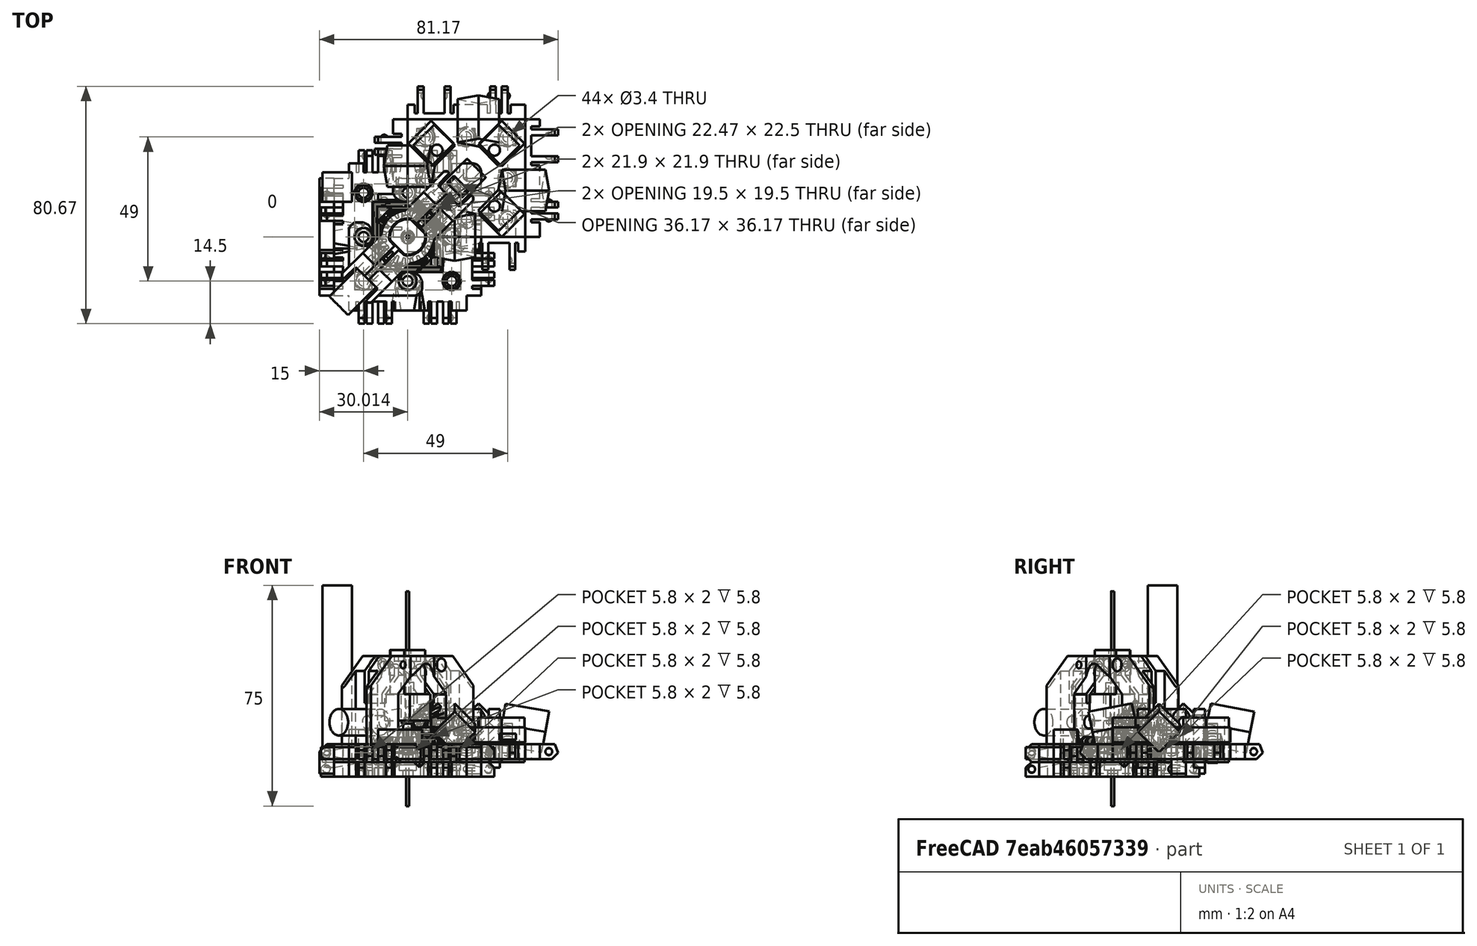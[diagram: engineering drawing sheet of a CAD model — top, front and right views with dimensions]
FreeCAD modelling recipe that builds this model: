
FCSTD DOCUMENT  (FreeCAD 0.18.4R)
Label: Robot-0.1
License: All rights reserved
LicenseURL: http://en.wikipedia.org/wiki/All_rights_reserved
objects: Part::Box×350, Part::Cut×132, Part::Sphere×107, Part::MultiFuse×98, Part::Cylinder×68, Part::Fuse×44, Part::Chamfer×23, Part::Feature×12, Drawing::FeatureViewAnnotation×10, Part::Fillet×7, App::DocumentObjectGroup×4, Part::MultiCommon×4, Drawing::FeaturePage×2, Part::FeaturePython×2, Part::Cone×2, Part::Mirroring×1
note: 850 computed .brp shape members not serialized (recipe doc carries the construction recipe); baked Part::Feature solids carry a one-line shape summary decoded from their .brp

FEATURE [Part::Box] Box  label="Cube"
  AttacherType = Attacher::AttachEngine3D
  Height = 5
  Length = 40
  Placement = pos=(-20,-20,-2) rot=(0,0,1;0rad)
  Width = 40
FEATURE [Part::Sphere] Sphere003  label="Mag Hole 3"
  Angle1 = -90
  Angle2 = 90
  Angle3 = 360
  AttacherType = Attacher::AttachEngine3D
  Placement = pos=(-15,15,1.7) rot=(0,0,1;0rad)
  Radius = 2.83
FEATURE [Part::Sphere] Sphere005  label="Mag Hole 2"
  Angle1 = -90
  Angle2 = 90
  Angle3 = 360
  AttacherType = Attacher::AttachEngine3D
  Placement = pos=(15,0,1.7) rot=(0,0,1;0rad)
  Radius = 2.825
FEATURE [Part::Sphere] Sphere  label="Mag Hole"
  Angle1 = -90
  Angle2 = 90
  Angle3 = 360
  AttacherType = Attacher::AttachEngine3D
  Placement = pos=(-15,-15,1.7) rot=(0,0,1;0rad)
  Radius = 2.83
FEATURE [Part::MultiFuse] Fusion004  label="Ball Holes"
  Shapes = -> [Sphere,Sphere005,Sphere003]
FEATURE [Part::Cut] Cut003
  Base = -> Box
  Tool = -> Fusion004
FEATURE [Part::Box] Box001  label="Cube001"
  AttacherType = Attacher::AttachEngine3D
  Height = 7
  Length = 5
  Placement = pos=(-5,0,-2) rot=(0,0,1;0rad)
  Width = 40
FEATURE [Part::Box] Box002  label="Cube002"
  AttacherType = Attacher::AttachEngine3D
  Height = 7
  Length = 10
  Placement = pos=(-15,6,-2) rot=(0,0,1;0rad)
  Width = 2
FEATURE [Part::Box] Box003  label="Cube003"
  AttacherType = Attacher::AttachEngine3D
  Height = 7
  Length = 10
  Placement = pos=(-15,10,-2) rot=(0,0,1;0rad)
  Width = 2
FEATURE [Part::Box] Box004  label="Cube004"
  AttacherType = Attacher::AttachEngine3D
  Height = 7
  Length = 10
  Placement = pos=(-15,25.4,-2) rot=(0,0,1;0rad)
  Width = 2
FEATURE [Part::Box] Box005  label="Cube005"
  AttacherType = Attacher::AttachEngine3D
  Height = 7
  Length = 10
  Placement = pos=(-15,34.6,-2) rot=(0,0,1;0rad)
  Width = 2
FEATURE [Part::Sphere] Sphere008
  Angle1 = -90
  Angle2 = 90
  Angle3 = 360
  AttacherType = Attacher::AttachEngine3D
  Placement = pos=(-7.5,6.5,0.5) rot=(0,0,1;0rad)
  Radius = 1.25
FEATURE [Part::Box] Box006  label="Chamfer Cube"
  AttacherType = Attacher::AttachEngine3D
  Height = 10
  Length = 13
  Placement = pos=(-11.69,0,-1.19) rot=(0,-1,0;0.785398rad)
  Width = 40
FEATURE [Part::Sphere] Sphere009
  Angle1 = -90
  Angle2 = 90
  Angle3 = 360
  AttacherType = Attacher::AttachEngine3D
  Placement = pos=(-7.5,11.5,0.5) rot=(0,0,1;0rad)
  Radius = 1.25
FEATURE [Part::Sphere] Sphere010
  Angle1 = -90
  Angle2 = 90
  Angle3 = 360
  AttacherType = Attacher::AttachEngine3D
  Placement = pos=(-7.5,28,0.5) rot=(0,0,1;0rad)
  Radius = 1.5
FEATURE [Part::Sphere] Sphere011
  Angle1 = -90
  Angle2 = 90
  Angle3 = 360
  AttacherType = Attacher::AttachEngine3D
  Placement = pos=(-7.5,34,0.5) rot=(0,0,1;0rad)
  Radius = 1.5
FEATURE [Part::Box] Box007  label="Cube007"
  AttacherType = Attacher::AttachEngine3D
  Height = 7
  Length = 4
  Placement = pos=(-6,5,-2) rot=(0,0,1;0rad)
  Width = 1
FEATURE [Part::Box] Box008  label="Cube008"
  AttacherType = Attacher::AttachEngine3D
  Height = 7
  Length = 4
  Placement = pos=(-6,8,-2) rot=(0,0,1;0rad)
  Width = 2
FEATURE [Part::Box] Box009  label="Cube009"
  AttacherType = Attacher::AttachEngine3D
  Height = 7
  Length = 4
  Placement = pos=(-6,12,-2) rot=(0,0,1;0rad)
  Width = 1
FEATURE [Part::Box] Box010  label="Cube010"
  AttacherType = Attacher::AttachEngine3D
  Height = 7
  Length = 4
  Placement = pos=(-6,24.4,-2) rot=(0,0,1;0rad)
  Width = 1
FEATURE [Part::Box] Box011  label="Cube011"
  AttacherType = Attacher::AttachEngine3D
  Height = 7
  Length = 4
  Placement = pos=(-6,36.6,-2) rot=(0,0,1;0rad)
  Width = 1
FEATURE [Part::Box] Box012  label="Cube012"
  AttacherType = Attacher::AttachEngine3D
  Height = 7
  Length = 4
  Placement = pos=(-6,27.4,-2) rot=(0,0,1;0rad)
  Width = 7.2
FEATURE [Part::MultiFuse] Fusion003  label="Extra Holes for Clips"
  Shapes = -> [Box012,Box009,Box011,Box008,Box010,Box007]
FEATURE [Part::Box] Box013  label="Re-level Edge Clip Block"
  AttacherType = Attacher::AttachEngine3D
  Height = 10
  Length = 20
  Placement = pos=(-19,-2,3) rot=(0,0,1;0rad)
  Width = 44
FEATURE [Part::Box] Box014  label="Cube014"
  AttacherType = Attacher::AttachEngine3D
  Height = 7
  Length = 10
  Placement = pos=(-10,34.6,0) rot=(0,0,1;0rad)
  Width = 2
FEATURE [Part::Box] Box015  label="Cube015"
  AttacherType = Attacher::AttachEngine3D
  Height = 7
  Length = 5
  Width = 40
FEATURE [Part::Box] Box016  label="Cube016"
  AttacherType = Attacher::AttachEngine3D
  Height = 7
  Length = 10
  Placement = pos=(-10,25.4,0) rot=(0,0,1;0rad)
  Width = 2
FEATURE [Part::Box] Box017  label="Cube017"
  AttacherType = Attacher::AttachEngine3D
  Height = 7
  Length = 10
  Placement = pos=(-10,10,0) rot=(0,0,1;0rad)
  Width = 2
FEATURE [Part::Box] Box018  label="Cube018"
  AttacherType = Attacher::AttachEngine3D
  Height = 7
  Length = 10
  Placement = pos=(-10,6,0) rot=(0,0,1;0rad)
  Width = 2
FEATURE [Part::Sphere] Sphere012
  Angle1 = -90
  Angle2 = 90
  Angle3 = 360
  AttacherType = Attacher::AttachEngine3D
  Placement = pos=(-3,6.5,2.5) rot=(0,0,1;0rad)
  Radius = 1.25
FEATURE [Part::Box] Box019  label="Cube019"
  AttacherType = Attacher::AttachEngine3D
  Height = 10
  Length = 13
  Placement = pos=(-10.19,0,-1.19) rot=(0,-1,0;0.785398rad)
  Width = 40
FEATURE [Part::Sphere] Sphere013
  Angle1 = -90
  Angle2 = 90
  Angle3 = 360
  AttacherType = Attacher::AttachEngine3D
  Placement = pos=(-3,11.5,2.5) rot=(0,0,1;0rad)
  Radius = 1.25
FEATURE [Part::Sphere] Sphere014
  Angle1 = -90
  Angle2 = 90
  Angle3 = 360
  AttacherType = Attacher::AttachEngine3D
  Placement = pos=(-3,28,2.5) rot=(0,0,1;0rad)
  Radius = 1.5
FEATURE [Part::Sphere] Sphere015
  Angle1 = -90
  Angle2 = 90
  Angle3 = 360
  AttacherType = Attacher::AttachEngine3D
  Placement = pos=(-3,34,2.5) rot=(0,0,1;0rad)
  Radius = 1.5
FEATURE [Part::MultiFuse] Fusion005
  Shapes = -> [Box015,Box018,Box017,Box016,Box014]
FEATURE [Part::Cut] Cut005
  Base = -> Fusion005
  Tool = -> Box019
FEATURE [Part::MultiFuse] Fusion006
  Shapes = -> [Sphere012,Sphere013,Cut005]
FEATURE [Part::MultiFuse] Fusion007
  Shapes = -> [Sphere015,Sphere014]
FEATURE [Part::Cut] Cut006
  Base = -> Fusion006
  Tool = -> Fusion007
FEATURE [Part::Chamfer] Chamfer002
  Base = -> Cut006
  Edges = 4 edges r=4: [Edge31,Edge37,Edge43,Edge46]
FEATURE [Part::Box] Box020  label="Cube020"
  AttacherType = Attacher::AttachEngine3D
  Height = 7
  Length = 4
  Placement = pos=(-1,5,0) rot=(0,0,1;0rad)
  Width = 1
FEATURE [Part::Box] Box021  label="Cube021"
  AttacherType = Attacher::AttachEngine3D
  Height = 7
  Length = 4
  Placement = pos=(-1,8,0) rot=(0,0,1;0rad)
  Width = 2
FEATURE [Part::Box] Box022  label="Cube022"
  AttacherType = Attacher::AttachEngine3D
  Height = 7
  Length = 4
  Placement = pos=(-1,12,0) rot=(0,0,1;0rad)
  Width = 1
FEATURE [Part::Box] Box023  label="Cube023"
  AttacherType = Attacher::AttachEngine3D
  Height = 7
  Length = 4
  Placement = pos=(-1,24.4,0) rot=(0,0,1;0rad)
  Width = 1
FEATURE [Part::Box] Box024  label="Cube024"
  AttacherType = Attacher::AttachEngine3D
  Height = 7
  Length = 4
  Placement = pos=(-1,36.6,0) rot=(0,0,1;0rad)
  Width = 1
FEATURE [Part::Box] Box025  label="Cube025"
  AttacherType = Attacher::AttachEngine3D
  Height = 7
  Length = 4
  Placement = pos=(-1,27.4,0) rot=(0,0,1;0rad)
  Width = 7.2
FEATURE [Part::MultiFuse] Fusion008
  Shapes = -> [Box025,Box022,Box024,Box021,Box023,Box020]
FEATURE [Part::Cut] Cut007
  Base = -> Chamfer002
  Placement = pos=(-5,40,3) rot=(1,0,0;3.14159rad)
  Tool = -> Fusion008
FEATURE [Part::Box] Box026  label="Cube026"
  AttacherType = Attacher::AttachEngine3D
  Height = 10
  Length = 12
  Placement = pos=(-11,-2,-12) rot=(0,0,1;0rad)
  Width = 44
FEATURE [Part::Cut] Cut008
  Base = -> Cut007
  Placement = pos=(40,0,0) rot=(0,0,1;1.5708rad)
  Tool = -> Box026
FEATURE [Part::Box] Box027  label="Cube027"
  AttacherType = Attacher::AttachEngine3D
  Height = 7
  Length = 4
  Placement = pos=(-1,12,0) rot=(0,0,1;0rad)
  Width = 1
FEATURE [Part::Box] Box028  label="Cube028"
  AttacherType = Attacher::AttachEngine3D
  Height = 10
  Length = 13
  Placement = pos=(-10.19,0,-1.19) rot=(0,-1,0;0.785398rad)
  Width = 40
FEATURE [Part::Box] Box029  label="Cube029"
  AttacherType = Attacher::AttachEngine3D
  Height = 7
  Length = 4
  Placement = pos=(-1,27.4,0) rot=(0,0,1;0rad)
  Width = 7.2
FEATURE [Part::Box] Box030  label="Cube030"
  AttacherType = Attacher::AttachEngine3D
  Height = 7
  Length = 4
  Placement = pos=(-1,5,0) rot=(0,0,1;0rad)
  Width = 1
FEATURE [Part::Box] Box031  label="Cube031"
  AttacherType = Attacher::AttachEngine3D
  Height = 7
  Length = 10
  Placement = pos=(-10,6,0) rot=(0,0,1;0rad)
  Width = 2
FEATURE [Part::Box] Box032  label="Cube032"
  AttacherType = Attacher::AttachEngine3D
  Height = 10
  Length = 12
  Placement = pos=(-11,-2,-12) rot=(0,0,1;0rad)
  Width = 44
FEATURE [Part::Sphere] Sphere016
  Angle1 = -90
  Angle2 = 90
  Angle3 = 360
  AttacherType = Attacher::AttachEngine3D
  Placement = pos=(-3,6.5,2.5) rot=(0,0,1;0rad)
  Radius = 1.25
FEATURE [Part::Box] Box033  label="Cube033"
  AttacherType = Attacher::AttachEngine3D
  Height = 7
  Length = 10
  Placement = pos=(-10,25.4,0) rot=(0,0,1;0rad)
  Width = 2
FEATURE [Part::Box] Box034  label="Cube034"
  AttacherType = Attacher::AttachEngine3D
  Height = 7
  Length = 10
  Placement = pos=(-10,10,0) rot=(0,0,1;0rad)
  Width = 2
FEATURE [Part::Sphere] Sphere017
  Angle1 = -90
  Angle2 = 90
  Angle3 = 360
  AttacherType = Attacher::AttachEngine3D
  Placement = pos=(-3,28,2.5) rot=(0,0,1;0rad)
  Radius = 1.5
FEATURE [Part::Sphere] Sphere018
  Angle1 = -90
  Angle2 = 90
  Angle3 = 360
  AttacherType = Attacher::AttachEngine3D
  Placement = pos=(-3,11.5,2.5) rot=(0,0,1;0rad)
  Radius = 1.25
FEATURE [Part::Box] Box035  label="Cube035"
  AttacherType = Attacher::AttachEngine3D
  Height = 7
  Length = 4
  Placement = pos=(-1,36.6,0) rot=(0,0,1;0rad)
  Width = 1
FEATURE [Part::Sphere] Sphere019
  Angle1 = -90
  Angle2 = 90
  Angle3 = 360
  AttacherType = Attacher::AttachEngine3D
  Placement = pos=(-3,34,2.5) rot=(0,0,1;0rad)
  Radius = 1.5
FEATURE [Part::MultiFuse] Fusion011
  Shapes = -> [Sphere019,Sphere017]
FEATURE [Part::Box] Box036  label="Cube036"
  AttacherType = Attacher::AttachEngine3D
  Height = 7
  Length = 4
  Placement = pos=(-1,8,0) rot=(0,0,1;0rad)
  Width = 2
FEATURE [Part::Box] Box037  label="Cube037"
  AttacherType = Attacher::AttachEngine3D
  Height = 7
  Length = 10
  Placement = pos=(-10,34.6,0) rot=(0,0,1;0rad)
  Width = 2
FEATURE [Part::Box] Box038  label="Cube038"
  AttacherType = Attacher::AttachEngine3D
  Height = 7
  Length = 4
  Placement = pos=(-1,24.4,0) rot=(0,0,1;0rad)
  Width = 1
FEATURE [Part::MultiFuse] Fusion009
  Shapes = -> [Box029,Box027,Box035,Box036,Box038,Box030]
FEATURE [Part::Box] Box039  label="Cube039"
  AttacherType = Attacher::AttachEngine3D
  Height = 7
  Length = 5
  Width = 40
FEATURE [Part::MultiFuse] Fusion012
  Shapes = -> [Box039,Box031,Box034,Box033,Box037]
FEATURE [Part::Cut] Cut011
  Base = -> Fusion012
  Tool = -> Box028
FEATURE [Part::MultiFuse] Fusion010
  Shapes = -> [Sphere016,Sphere018,Cut011]
FEATURE [Part::Cut] Cut012
  Base = -> Fusion010
  Tool = -> Fusion011
FEATURE [Part::Chamfer] Chamfer003
  Base = -> Cut012
  Edges = 4 edges r=4: [Edge31,Edge37,Edge43,Edge46]
FEATURE [Part::Cut] Cut010
  Base = -> Chamfer003
  Placement = pos=(-5,40,3) rot=(1,0,0;3.14159rad)
  Tool = -> Fusion009
FEATURE [Part::Cut] Cut009
  Base = -> Cut010
  Placement = pos=(40,40,0) rot=(0,0,1;3.14159rad)
  Tool = -> Box032
FEATURE [Part::Sphere] Sphere020
  Angle1 = -90
  Angle2 = 90
  Angle3 = 360
  AttacherType = Attacher::AttachEngine3D
  Placement = pos=(-3,11.5,2.5) rot=(0,0,1;0rad)
  Radius = 1.25
FEATURE [Part::Box] Box040  label="Cube040"
  AttacherType = Attacher::AttachEngine3D
  Height = 7
  Length = 10
  Placement = pos=(-10,6,0) rot=(0,0,1;0rad)
  Width = 2
FEATURE [Part::Box] Box041  label="Cube041"
  AttacherType = Attacher::AttachEngine3D
  Height = 7
  Length = 4
  Placement = pos=(-1,8,0) rot=(0,0,1;0rad)
  Width = 2
FEATURE [Part::Box] Box042  label="Cube042"
  AttacherType = Attacher::AttachEngine3D
  Height = 7
  Length = 10
  Placement = pos=(-10,10,0) rot=(0,0,1;0rad)
  Width = 2
FEATURE [Part::Box] Box043  label="Cube043"
  AttacherType = Attacher::AttachEngine3D
  Height = 10
  Length = 12
  Placement = pos=(-11,-2,-12) rot=(0,0,1;0rad)
  Width = 44
FEATURE [Part::Box] Box044  label="Cube044"
  AttacherType = Attacher::AttachEngine3D
  Height = 7
  Length = 4
  Placement = pos=(-1,5,0) rot=(0,0,1;0rad)
  Width = 1
FEATURE [Part::Sphere] Sphere021
  Angle1 = -90
  Angle2 = 90
  Angle3 = 360
  AttacherType = Attacher::AttachEngine3D
  Placement = pos=(-3,28,2.5) rot=(0,0,1;0rad)
  Radius = 1.5
FEATURE [Part::Sphere] Sphere022
  Angle1 = -90
  Angle2 = 90
  Angle3 = 360
  AttacherType = Attacher::AttachEngine3D
  Placement = pos=(-3,6.5,2.5) rot=(0,0,1;0rad)
  Radius = 1.25
FEATURE [Part::Sphere] Sphere023
  Angle1 = -90
  Angle2 = 90
  Angle3 = 360
  AttacherType = Attacher::AttachEngine3D
  Placement = pos=(-3,34,2.5) rot=(0,0,1;0rad)
  Radius = 1.5
FEATURE [Part::Box] Box045  label="Cube045"
  AttacherType = Attacher::AttachEngine3D
  Height = 7
  Length = 4
  Placement = pos=(-1,12,0) rot=(0,0,1;0rad)
  Width = 1
FEATURE [Part::Box] Box046  label="Cube046"
  AttacherType = Attacher::AttachEngine3D
  Height = 7
  Length = 5
  Width = 40
FEATURE [Part::Box] Box047  label="Cube047"
  AttacherType = Attacher::AttachEngine3D
  Height = 7
  Length = 4
  Placement = pos=(-1,36.6,0) rot=(0,0,1;0rad)
  Width = 1
FEATURE [Part::Box] Box048  label="Cube048"
  AttacherType = Attacher::AttachEngine3D
  Height = 7
  Length = 4
  Placement = pos=(-1,24.4,0) rot=(0,0,1;0rad)
  Width = 1
FEATURE [Part::Box] Box049  label="Cube049"
  AttacherType = Attacher::AttachEngine3D
  Height = 7
  Length = 10
  Placement = pos=(-10,25.4,0) rot=(0,0,1;0rad)
  Width = 2
FEATURE [Part::Box] Box050  label="Cube050"
  AttacherType = Attacher::AttachEngine3D
  Height = 10
  Length = 13
  Placement = pos=(-10.19,0,-1.19) rot=(0,-1,0;0.785398rad)
  Width = 40
FEATURE [Part::Box] Box051  label="Cube051"
  AttacherType = Attacher::AttachEngine3D
  Height = 7
  Length = 10
  Placement = pos=(-10,34.6,0) rot=(0,0,1;0rad)
  Width = 2
FEATURE [Part::MultiFuse] Fusion015
  Shapes = -> [Box046,Box040,Box042,Box049,Box051]
FEATURE [Part::Cut] Cut013
  Base = -> Fusion015
  Tool = -> Box050
FEATURE [Part::MultiFuse] Fusion013
  Shapes = -> [Sphere022,Sphere020,Cut013]
FEATURE [Part::MultiFuse] Fusion016
  Shapes = -> [Sphere023,Sphere021]
FEATURE [Part::Cut] Cut014
  Base = -> Fusion013
  Tool = -> Fusion016
FEATURE [Part::Chamfer] Chamfer004
  Base = -> Cut014
  Edges = 4 edges r=4: [Edge31,Edge37,Edge43,Edge46]
FEATURE [Part::Box] Box052  label="Cube052"
  AttacherType = Attacher::AttachEngine3D
  Height = 7
  Length = 4
  Placement = pos=(-1,27.4,0) rot=(0,0,1;0rad)
  Width = 7.2
FEATURE [Part::MultiFuse] Fusion014
  Shapes = -> [Box052,Box045,Box047,Box041,Box048,Box044]
FEATURE [Part::Cut] Cut016
  Base = -> Chamfer004
  Placement = pos=(-5,40,3) rot=(1,0,0;3.14159rad)
  Tool = -> Fusion014
FEATURE [Part::Cut] Cut015
  Base = -> Cut016
  Placement = pos=(0,40,0) rot=(0,0,-1;1.5708rad)
  Tool = -> Box043
FEATURE [Part::Box] Box054  label="Cube054"
  AttacherType = Attacher::AttachEngine3D
  Height = 15
  Length = 10
  Placement = pos=(9,2,-3) rot=(0,0,1;0.785398rad)
  Width = 10
FEATURE [Part::Box] Box055  label="Cube055"
  AttacherType = Attacher::AttachEngine3D
  Height = 15
  Length = 10
  Placement = pos=(31,24,-3) rot=(0,0,1;0.785398rad)
  Width = 10
FEATURE [Part::Box] Box056  label="Cube056"
  AttacherType = Attacher::AttachEngine3D
  Height = 15
  Length = 10
  Placement = pos=(31,2,-3) rot=(0,0,1;0.785398rad)
  Width = 10
FEATURE [Part::Box] Box057  label="Cube057"
  AttacherType = Attacher::AttachEngine3D
  Height = 15
  Length = 10
  Placement = pos=(9,24,-3) rot=(0,0,1;0.785398rad)
  Width = 10
FEATURE [Part::MultiFuse] Fusion017
  Shapes = -> [Box054,Box057,Box056,Box055]
FEATURE [Part::Box] Box058  label="Cube058"
  AttacherType = Attacher::AttachEngine3D
  Height = 5
  Length = 40
  Placement = pos=(0,0,3.7) rot=(0,0,1;0rad)
  Width = 40
FEATURE [Part::Box] Box059  label="Square Nut Hole 008"
  AttacherType = Attacher::AttachEngine3D
  Height = 2
  Length = 5.6
  Placement = pos=(17.2,31.2,4.6) rot=(0,0,1;0rad)
  Width = 5.6
FEATURE [Part::Box] Box060  label="Square Nut Hole 009"
  AttacherType = Attacher::AttachEngine3D
  Height = 2
  Length = 5.6
  Placement = pos=(17.2,-0.85,4.6) rot=(0,0,1;0rad)
  Width = 10
FEATURE [Part::Box] Box061  label="Square Nut Hole 010"
  AttacherType = Attacher::AttachEngine3D
  Height = 2
  Length = 5.6
  Placement = pos=(31.2,-0.85,4.6) rot=(0,0,1;0rad)
  Width = 10
FEATURE [Part::Box] Box062  label="Square Nut Hole 011"
  AttacherType = Attacher::AttachEngine3D
  Height = 2
  Length = 5.4
  Placement = pos=(31.3,17.3,4.6) rot=(0,0,1;0rad)
  Width = 5.4
FEATURE [Part::Box] Box063  label="Square Nut Hole 012"
  AttacherType = Attacher::AttachEngine3D
  Height = 2
  Length = 5.7
  Placement = pos=(3.15,31.15,4.6) rot=(0,0,1;0rad)
  Width = 5.7
FEATURE [Part::Box] Box064  label="Square Nut Hole 013"
  AttacherType = Attacher::AttachEngine3D
  Height = 2
  Length = 5.5
  Placement = pos=(31.25,31.25,4.6) rot=(0,0,1;0rad)
  Width = 5.5
FEATURE [Part::Box] Box065  label="Square Nut Hole 014"
  AttacherType = Attacher::AttachEngine3D
  Height = 2
  Length = 5.8
  Placement = pos=(3.1,17.1,4.6) rot=(0,0,1;0rad)
  Width = 5.8
FEATURE [Part::Box] Box066  label="Square Nut Hole 015"
  AttacherType = Attacher::AttachEngine3D
  Height = 2
  Length = 5.6
  Placement = pos=(3.2,-0.85,4.6) rot=(0,0,1;0rad)
  Width = 10
FEATURE [Part::Sphere] Sphere006  label="Nut Clearence1"
  Angle1 = -90
  Angle2 = 90
  Angle3 = 360
  AttacherType = Attacher::AttachEngine3D
  Placement = pos=(6,6,2.4) rot=(0,0,1;0rad)
  Radius = 3.35
FEATURE [Part::Sphere] Sphere024
  Angle1 = -90
  Angle2 = 90
  Angle3 = 360
  AttacherType = Attacher::AttachEngine3D
  Placement = pos=(6,34,2.4) rot=(0,0,1;0rad)
  Radius = 3.35
FEATURE [Part::Sphere] Sphere007
  Angle1 = -90
  Angle2 = 90
  Angle3 = 360
  AttacherType = Attacher::AttachEngine3D
  Placement = pos=(34,20,2.4) rot=(0,0,1;0rad)
  Radius = 3.35
FEATURE [Part::Sphere] Sphere001
  Angle1 = -90
  Angle2 = 90
  Angle3 = 360
  AttacherType = Attacher::AttachEngine3D
  Placement = pos=(34,6,2.4) rot=(0,0,1;0rad)
  Radius = 3.35
FEATURE [Part::Sphere] Sphere025
  Angle1 = -90
  Angle2 = 90
  Angle3 = 360
  AttacherType = Attacher::AttachEngine3D
  Placement = pos=(20,6,2.4) rot=(0,0,1;0rad)
  Radius = 3.35
FEATURE [Part::Sphere] Sphere026
  Angle1 = -90
  Angle2 = 90
  Angle3 = 360
  AttacherType = Attacher::AttachEngine3D
  Placement = pos=(20,34,2.4) rot=(0,0,1;0rad)
  Radius = 3.35
FEATURE [Part::Sphere] Sphere004
  Angle1 = -90
  Angle2 = 90
  Angle3 = 360
  AttacherType = Attacher::AttachEngine3D
  Placement = pos=(6,20,2.4) rot=(0,0,1;0rad)
  Radius = 3.35
FEATURE [Part::Sphere] Sphere002
  Angle1 = -90
  Angle2 = 90
  Angle3 = 360
  AttacherType = Attacher::AttachEngine3D
  Placement = pos=(34,34,2.4) rot=(0,0,1;0rad)
  Radius = 3.35
FEATURE [Part::Cylinder] Cylinder
  Angle = 360
  AttacherType = Attacher::AttachEngine3D
  Height = 10
  Placement = pos=(6,6,0) rot=(0,0,1;0rad)
  Radius = 1.7
FEATURE [Part::Cylinder] Cylinder002
  Angle = 360
  AttacherType = Attacher::AttachEngine3D
  Height = 10
  Placement = pos=(34,6,0) rot=(0,0,1;0rad)
  Radius = 1.7
FEATURE [Part::Cylinder] Cylinder001
  Angle = 360
  AttacherType = Attacher::AttachEngine3D
  Height = 10
  Placement = pos=(20,6,0) rot=(0,0,1;0rad)
  Radius = 1.7
FEATURE [Part::Cylinder] Cylinder003
  Angle = 360
  AttacherType = Attacher::AttachEngine3D
  Height = 10
  Placement = pos=(34,34,0) rot=(0,0,1;0rad)
  Radius = 1.7
FEATURE [Part::Cylinder] Cylinder004
  Angle = 360
  AttacherType = Attacher::AttachEngine3D
  Height = 10
  Placement = pos=(20,34,0) rot=(0,0,1;0rad)
  Radius = 1.7
FEATURE [Part::Cylinder] Cylinder005
  Angle = 360
  AttacherType = Attacher::AttachEngine3D
  Height = 10
  Placement = pos=(6,34,0) rot=(0,0,1;0rad)
  Radius = 1.7
FEATURE [Part::Cylinder] Cylinder006
  Angle = 360
  AttacherType = Attacher::AttachEngine3D
  Height = 10
  Placement = pos=(6,20,0) rot=(0,0,1;0rad)
  Radius = 1.7
FEATURE [Part::Cylinder] Cylinder007
  Angle = 360
  AttacherType = Attacher::AttachEngine3D
  Height = 10
  Placement = pos=(34,20,0) rot=(0,0,1;0rad)
  Radius = 1.7
FEATURE [Part::MultiFuse] Fusion018
  Shapes = -> [Cylinder,Cylinder004,Cylinder007,Cylinder005,Cylinder006,Cylinder001,Cylinder002,Cylinder003]
FEATURE [Part::MultiFuse] Fusion019
  Shapes = -> [Sphere007,Sphere024,Sphere006,Sphere025,Sphere001,Sphere026,Sphere004,Sphere002]
FEATURE [Part::MultiFuse] Fusion020
  Shapes = -> [Box061,Box065,Box062,Box063,Box064,Box066,Box059,Box060]
FEATURE [Part::Cut] Cut017
  Base = -> Box058
  Tool = -> Fusion020
FEATURE [Part::Cut] Cut019
  Base = -> Cut017
  Tool = -> Fusion019
FEATURE [Part::Cut] Cut018
  Base = -> Cut019
  Tool = -> Fusion018
FEATURE [Part::Cylinder] Cylinder008
  Angle = 360
  AttacherType = Attacher::AttachEngine3D
  Height = 20
  Placement = pos=(10,10.5,-5) rot=(0,0,1;0rad)
  Radius = 1.9
FEATURE [Part::Cylinder] Cylinder009
  Angle = 360
  AttacherType = Attacher::AttachEngine3D
  Height = 20
  Placement = pos=(29.5,10.5,-5) rot=(0,0,1;0rad)
  Radius = 1.9
FEATURE [Part::Cylinder] Cylinder010
  Angle = 360
  AttacherType = Attacher::AttachEngine3D
  Height = 20
  Placement = pos=(29.5,29.5,-5) rot=(0,0,1;0rad)
  Radius = 1.9
FEATURE [Part::Cylinder] Cylinder011
  Angle = 360
  AttacherType = Attacher::AttachEngine3D
  Height = 20
  Placement = pos=(10,29.5,-7) rot=(0,0,1;0rad)
  Radius = 1.9
FEATURE [Part::MultiFuse] Fusion021  label="M2 Screw holes"
  Shapes = -> [Cylinder008,Cylinder009,Cylinder011,Cylinder010]
FEATURE [Part::Box] Box067  label="Square Nut Hole 016"
  AttacherType = Attacher::AttachEngine3D
  Height = 2
  Length = 5.8
  Placement = pos=(31.1,17.1,4.6) rot=(0,0,1;0rad)
  Width = 5.8
FEATURE [Part::Box] Box068  label="Square Nut Hole 017"
  AttacherType = Attacher::AttachEngine3D
  Height = 2
  Length = 5.8
  Placement = pos=(17.1,36.9,2.1) rot=(1,0,0;3.14159rad)
  Width = 5.8
FEATURE [Part::Box] Box069  label="Square Nut Hole 018"
  AttacherType = Attacher::AttachEngine3D
  Height = 2
  Length = 5.8
  Placement = pos=(-2.9,2.9,2.1) rot=(1,0,0;3.14159rad)
  Width = 5.8
FEATURE [Part::Box] Box070  label="Square Nut Hole 019"
  AttacherType = Attacher::AttachEngine3D
  Height = 2
  Length = 5.8
  Placement = pos=(3.1,3.1,4.6) rot=(0,0,1;0rad)
  Width = 5.8
FEATURE [Part::Box] Box071  label="Square Nut Hole 020"
  AttacherType = Attacher::AttachEngine3D
  Height = 2
  Length = 5.8
  Placement = pos=(3.1,31.1,4.6) rot=(0,0,1;0rad)
  Width = 5.8
FEATURE [Part::Box] Box072  label="Square Nut Hole 021"
  AttacherType = Attacher::AttachEngine3D
  Height = 2
  Length = 5.8
  Placement = pos=(17.1,31.1,4.6) rot=(0,0,1;0rad)
  Width = 5.8
FEATURE [Part::Box] Box073  label="Square Nut Hole 022"
  AttacherType = Attacher::AttachEngine3D
  Height = 2
  Length = 5.8
  Placement = pos=(31.1,31.1,4.6) rot=(0,0,1;0rad)
  Width = 5.8
FEATURE [Part::Box] Box074  label="Square Nut Hole 023"
  AttacherType = Attacher::AttachEngine3D
  Height = 2
  Length = 5.8
  Placement = pos=(3.1,17.1,4.6) rot=(0,0,1;0rad)
  Width = 5.8
FEATURE [Part::Cylinder] Cylinder012
  Angle = 360
  AttacherType = Attacher::AttachEngine3D
  Height = 10
  Placement = pos=(6,6,0) rot=(0,0,1;0rad)
  Radius = 1.7
FEATURE [Part::Cylinder] Cylinder013
  Angle = 360
  AttacherType = Attacher::AttachEngine3D
  Height = 10
  Placement = pos=(34,34,0) rot=(0,0,1;0rad)
  Radius = 1.7
FEATURE [Part::Cylinder] Cylinder014
  Angle = 360
  AttacherType = Attacher::AttachEngine3D
  Height = 10
  Placement = pos=(20,34,0) rot=(0,0,1;0rad)
  Radius = 1.7
FEATURE [Part::Cylinder] Cylinder015
  Angle = 360
  AttacherType = Attacher::AttachEngine3D
  Height = 10
  Placement = pos=(6,34,0) rot=(0,0,1;0rad)
  Radius = 1.7
FEATURE [Part::Cylinder] Cylinder016
  Angle = 360
  AttacherType = Attacher::AttachEngine3D
  Height = 10
  Placement = pos=(6,20,0) rot=(0,0,1;0rad)
  Radius = 1.7
FEATURE [Part::Cylinder] Cylinder017
  Angle = 360
  AttacherType = Attacher::AttachEngine3D
  Height = 10
  Placement = pos=(34,20,0) rot=(0,0,1;0rad)
  Radius = 1.7
FEATURE [Part::Cylinder] Cylinder018
  Angle = 360
  AttacherType = Attacher::AttachEngine3D
  Height = 10
  Placement = pos=(0,0,6.7) rot=(1,0,0;3.14159rad)
  Radius = 1.7
FEATURE [Part::Cylinder] Cylinder019
  Angle = 360
  AttacherType = Attacher::AttachEngine3D
  Height = 10
  Placement = pos=(20,34,6.7) rot=(1,0,0;3.14159rad)
  Radius = 1.7
FEATURE [Part::Box] Box075  label="Cube059"
  AttacherType = Attacher::AttachEngine3D
  Height = 5
  Length = 40
  Placement = pos=(-20,-20,-2) rot=(0,0,1;0rad)
  Width = 40
FEATURE [Part::Sphere] Sphere027
  Angle1 = -90
  Angle2 = 90
  Angle3 = 360
  AttacherType = Attacher::AttachEngine3D
  Placement = pos=(34,20,2.4) rot=(0,0,1;0rad)
  Radius = 3.35
FEATURE [Part::Sphere] Sphere028  label="Nut Clearence002"
  Angle1 = -90
  Angle2 = 90
  Angle3 = 360
  AttacherType = Attacher::AttachEngine3D
  Placement = pos=(6,6,2.4) rot=(0,0,1;0rad)
  Radius = 3.35
FEATURE [Part::Sphere] Sphere029
  Angle1 = -90
  Angle2 = 90
  Angle3 = 360
  AttacherType = Attacher::AttachEngine3D
  Placement = pos=(34,34,2.4) rot=(0,0,1;0rad)
  Radius = 3.35
FEATURE [Part::Sphere] Sphere030
  Angle1 = -90
  Angle2 = 90
  Angle3 = 360
  AttacherType = Attacher::AttachEngine3D
  Placement = pos=(0,0,4.3) rot=(1,0,0;3.14159rad)
  Radius = 3.35
FEATURE [Part::Sphere] Sphere031
  Angle1 = -90
  Angle2 = 90
  Angle3 = 360
  AttacherType = Attacher::AttachEngine3D
  Placement = pos=(20,34,4.3) rot=(1,0,0;3.14159rad)
  Radius = 3.35
FEATURE [Part::Sphere] Sphere032
  Angle1 = -90
  Angle2 = 90
  Angle3 = 360
  AttacherType = Attacher::AttachEngine3D
  Placement = pos=(6,34,2.4) rot=(0,0,1;0rad)
  Radius = 3.35
FEATURE [Part::Sphere] Sphere033
  Angle1 = -90
  Angle2 = 90
  Angle3 = 360
  AttacherType = Attacher::AttachEngine3D
  Placement = pos=(6,20,2.4) rot=(0,0,1;0rad)
  Radius = 3.35
FEATURE [Part::Sphere] Sphere034
  Angle1 = -90
  Angle2 = 90
  Angle3 = 360
  AttacherType = Attacher::AttachEngine3D
  Placement = pos=(20,34,2.4) rot=(0,0,1;0rad)
  Radius = 3.35
FEATURE [Part::Box] Box076  label="Cube060"
  AttacherType = Attacher::AttachEngine3D
  Height = 15
  Length = 19.5
  Placement = pos=(-9.75,-9.75,-3) rot=(0,0,1;0rad)
  Width = 19.5
FEATURE [Part::Box] Box077  label="Cube061"
  AttacherType = Attacher::AttachEngine3D
  Height = 15
  Length = 11
  Placement = pos=(8,24,-3) rot=(0,0,1;0.785398rad)
  Width = 11
FEATURE [Part::Box] Box078  label="Cube062"
  AttacherType = Attacher::AttachEngine3D
  Height = 15
  Length = 11
  Placement = pos=(8,0,-3) rot=(0,0,1;0.785398rad)
  Width = 11
FEATURE [Part::Box] Box079  label="Cube063"
  AttacherType = Attacher::AttachEngine3D
  Height = 15
  Length = 11
  Placement = pos=(32,0,-3) rot=(0,0,1;0.785398rad)
  Width = 11
FEATURE [Part::Box] Box080  label="Cube064"
  AttacherType = Attacher::AttachEngine3D
  Height = 15
  Length = 11
  Placement = pos=(32,24,-3) rot=(0,0,1;0.785398rad)
  Width = 11
FEATURE [Part::MultiFuse] Fusion022
  Shapes = -> [Box078,Box077,Box079,Box080]
FEATURE [Part::Cylinder] Cylinder020
  Angle = 360
  AttacherType = Attacher::AttachEngine3D
  Height = 20
  Placement = pos=(29.5,10.5,-5) rot=(0,0,1;0rad)
  Radius = 1.9
FEATURE [Part::Cylinder] Cylinder021
  Angle = 360
  AttacherType = Attacher::AttachEngine3D
  Height = 20
  Placement = pos=(10,29.5,-7) rot=(0,0,1;0rad)
  Radius = 1.9
FEATURE [Part::Cylinder] Cylinder022
  Angle = 360
  AttacherType = Attacher::AttachEngine3D
  Height = 20
  Placement = pos=(10,10.5,-5) rot=(0,0,1;0rad)
  Radius = 1.9
FEATURE [Part::Cylinder] Cylinder023
  Angle = 360
  AttacherType = Attacher::AttachEngine3D
  Height = 20
  Placement = pos=(29.5,29.5,-5) rot=(0,0,1;0rad)
  Radius = 1.9
FEATURE [Part::MultiFuse] Fusion023  label="M2 Screw holes001"
  Shapes = -> [Cylinder022,Cylinder020,Cylinder021,Cylinder023]
FEATURE [App::DocumentObjectGroup] Group  label="Cubes"
  Group = -> [Fusion017,Fusion022]
FEATURE [Part::Box] Box083  label="Cube067"
  AttacherType = Attacher::AttachEngine3D
  Height = 10
  Length = 24
  Placement = pos=(-12,-12,2.1) rot=(0,0,1;0rad)
  Width = 24
FEATURE [Part::Box] Box084  label="Cube068"
  AttacherType = Attacher::AttachEngine3D
  Height = 14
  Length = 20
  Placement = pos=(-10,-10,0) rot=(0,0,1;0rad)
  Width = 20
FEATURE [Part::Cut] Cut020
  Base = -> Box083
  Tool = -> Box084
FEATURE [Part::Chamfer] Chamfer007  label="Glue Channel Ball"
  Base = -> Cut020
  Edges = 8 edges r=0.95: [Edge4,Edge5,Edge14,Edge16,Edge17,Edge18,Edge19,Edge20]
FEATURE [Part::Chamfer] Chamfer008  label="Octogon Ball"
  Base = -> Box076
  Edges = 4 edges r=4: [Edge1,Edge3,Edge5,Edge7]
FEATURE [Part::Box] Box085  label="Cube069"
  AttacherType = Attacher::AttachEngine3D
  Height = 15
  Length = 19.5
  Placement = pos=(-9.75,-9.75,-14) rot=(0,0,1;0rad)
  Width = 19.5
FEATURE [Part::Box] Box086  label="Cube070"
  AttacherType = Attacher::AttachEngine3D
  Height = 10
  Length = 10
  Placement = pos=(4,-26,1) rot=(0.205904,-0.974848,-0.085288;0.803573rad)
  Width = 15
FEATURE [Part::Box] Box089  label="Cube073"
  AttacherType = Attacher::AttachEngine3D
  Height = 10
  Length = 10
  Placement = pos=(17,32.0919,9.95) rot=(-0.225436,0.969773,-0.093378;0.807337rad)
  Width = 15
FEATURE [Part::Box] Box090  label="Cube074"
  AttacherType = Attacher::AttachEngine3D
  Height = 10
  Length = 15
  Placement = pos=(30.8481,15.8,2.86019) rot=(0.974848,0.205904,-0.085288;0.803573rad)
  Width = 10
FEATURE [Part::Box] Box091  label="Cube075"
  AttacherType = Attacher::AttachEngine3D
  Height = 10
  Length = 10
  Placement = pos=(7.9081,17,9.95) rot=(-0.450607,0.280623,0.847469;1.65638rad)
  Width = 15
FEATURE [Part::Box] Box092  label="Cube076"
  AttacherType = Attacher::AttachEngine3D
  Height = 10
  Length = 10
  Placement = pos=(23,7.9081,9.95) rot=(-0.381178,-0.08861,0.920245;3.06822rad)
  Width = 15
FEATURE [Part::Box] Box093  label="Cube077"
  AttacherType = Attacher::AttachEngine3D
  Height = 7
  Length = 5
  Width = 40
FEATURE [Part::Box] Box094  label="Cube078"
  AttacherType = Attacher::AttachEngine3D
  Height = 7
  Length = 10
  Placement = pos=(-10,6,0) rot=(0,0,1;0rad)
  Width = 2
FEATURE [Part::Box] Box095  label="Cube079"
  AttacherType = Attacher::AttachEngine3D
  Height = 7
  Length = 10
  Placement = pos=(-10,10,0) rot=(0,0,1;0rad)
  Width = 2
FEATURE [Part::Box] Box096  label="Cube080"
  AttacherType = Attacher::AttachEngine3D
  Height = 7
  Length = 10
  Placement = pos=(-10,25.4,0) rot=(0,0,1;0rad)
  Width = 2
FEATURE [Part::Box] Box097  label="Cube081"
  AttacherType = Attacher::AttachEngine3D
  Height = 7
  Length = 10
  Placement = pos=(-10,34.6,0) rot=(0,0,1;0rad)
  Width = 2
FEATURE [Part::Sphere] Sphere035
  Angle1 = -90
  Angle2 = 90
  Angle3 = 360
  AttacherType = Attacher::AttachEngine3D
  Placement = pos=(-3,6.5,2.5) rot=(0,0,1;0rad)
  Radius = 1.25
FEATURE [Part::Box] Box098  label="Cube082"
  AttacherType = Attacher::AttachEngine3D
  Height = 10
  Length = 13
  Placement = pos=(-10.19,0,-1.19) rot=(0,-1,0;0.785398rad)
  Width = 40
FEATURE [Part::Sphere] Sphere036
  Angle1 = -90
  Angle2 = 90
  Angle3 = 360
  AttacherType = Attacher::AttachEngine3D
  Placement = pos=(-3,11.5,2.5) rot=(0,0,1;0rad)
  Radius = 1.25
FEATURE [Part::Sphere] Sphere037
  Angle1 = -90
  Angle2 = 90
  Angle3 = 360
  AttacherType = Attacher::AttachEngine3D
  Placement = pos=(-3,28,2.5) rot=(0,0,1;0rad)
  Radius = 1.5
FEATURE [Part::Sphere] Sphere038
  Angle1 = -90
  Angle2 = 90
  Angle3 = 360
  AttacherType = Attacher::AttachEngine3D
  Placement = pos=(-3,34,2.5) rot=(0,0,1;0rad)
  Radius = 1.5
FEATURE [Part::MultiFuse] Fusion030
  Shapes = -> [Box093,Box094,Box095,Box096,Box097]
FEATURE [Part::Cut] Cut025
  Base = -> Fusion030
  Tool = -> Box098
FEATURE [Part::MultiFuse] Fusion031
  Shapes = -> [Sphere035,Sphere036,Cut025]
FEATURE [Part::MultiFuse] Fusion032
  Shapes = -> [Sphere038,Sphere037]
FEATURE [Part::Cut] Cut026
  Base = -> Fusion031
  Tool = -> Fusion032
FEATURE [Part::Chamfer] Chamfer009
  Base = -> Cut026
  Edges = 4 edges r=4: [Edge31,Edge37,Edge43,Edge46]
FEATURE [Part::Box] Box099  label="Cube083"
  AttacherType = Attacher::AttachEngine3D
  Height = 7
  Length = 4
  Placement = pos=(-1,5,0) rot=(0,0,1;0rad)
  Width = 1
FEATURE [Part::Box] Box100  label="Cube084"
  AttacherType = Attacher::AttachEngine3D
  Height = 7
  Length = 4
  Placement = pos=(-1,8,0) rot=(0,0,1;0rad)
  Width = 2
FEATURE [Part::Box] Box101  label="Cube085"
  AttacherType = Attacher::AttachEngine3D
  Height = 7
  Length = 4
  Placement = pos=(-1,12,0) rot=(0,0,1;0rad)
  Width = 1
FEATURE [Part::Box] Box102  label="Cube086"
  AttacherType = Attacher::AttachEngine3D
  Height = 7
  Length = 4
  Placement = pos=(-1,24.4,0) rot=(0,0,1;0rad)
  Width = 1
FEATURE [Part::Box] Box103  label="Cube087"
  AttacherType = Attacher::AttachEngine3D
  Height = 7
  Length = 4
  Placement = pos=(-1,36.6,0) rot=(0,0,1;0rad)
  Width = 1
FEATURE [Part::Box] Box104  label="Cube088"
  AttacherType = Attacher::AttachEngine3D
  Height = 7
  Length = 4
  Placement = pos=(-1,27.4,0) rot=(0,0,1;0rad)
  Width = 7.2
FEATURE [Part::MultiFuse] Fusion033
  Shapes = -> [Box104,Box101,Box103,Box100,Box102,Box099]
FEATURE [Part::Cut] Cut027
  Base = -> Chamfer009
  Placement = pos=(-5,40,3) rot=(1,0,0;3.14159rad)
  Tool = -> Fusion033
FEATURE [Part::Box] Box105  label="Cube089"
  AttacherType = Attacher::AttachEngine3D
  Height = 10
  Length = 12
  Placement = pos=(-11,-2,-12) rot=(0,0,1;0rad)
  Width = 44
FEATURE [Part::Cut] Cut028
  Base = -> Cut027
  Tool = -> Box105
FEATURE [Part::Box] Box106  label="Cube090"
  AttacherType = Attacher::AttachEngine3D
  Height = 7
  Length = 10
  Placement = pos=(-10,34.6,0) rot=(0,0,1;0rad)
  Width = 2
FEATURE [Part::Box] Box107  label="Cube091"
  AttacherType = Attacher::AttachEngine3D
  Height = 7
  Length = 5
  Width = 40
FEATURE [Part::Box] Box108  label="Cube092"
  AttacherType = Attacher::AttachEngine3D
  Height = 7
  Length = 10
  Placement = pos=(-10,25.4,0) rot=(0,0,1;0rad)
  Width = 2
FEATURE [Part::Box] Box109  label="Cube093"
  AttacherType = Attacher::AttachEngine3D
  Height = 7
  Length = 10
  Placement = pos=(-10,10,0) rot=(0,0,1;0rad)
  Width = 2
FEATURE [Part::Box] Box110  label="Cube094"
  AttacherType = Attacher::AttachEngine3D
  Height = 7
  Length = 10
  Placement = pos=(-10,6,0) rot=(0,0,1;0rad)
  Width = 2
FEATURE [Part::Sphere] Sphere039
  Angle1 = -90
  Angle2 = 90
  Angle3 = 360
  AttacherType = Attacher::AttachEngine3D
  Placement = pos=(-3,6.5,2.5) rot=(0,0,1;0rad)
  Radius = 1.25
FEATURE [Part::Box] Box111  label="Cube095"
  AttacherType = Attacher::AttachEngine3D
  Height = 10
  Length = 13
  Placement = pos=(-10.19,0,-1.19) rot=(0,-1,0;0.785398rad)
  Width = 40
FEATURE [Part::Sphere] Sphere040
  Angle1 = -90
  Angle2 = 90
  Angle3 = 360
  AttacherType = Attacher::AttachEngine3D
  Placement = pos=(-3,11.5,2.5) rot=(0,0,1;0rad)
  Radius = 1.25
FEATURE [Part::Sphere] Sphere041
  Angle1 = -90
  Angle2 = 90
  Angle3 = 360
  AttacherType = Attacher::AttachEngine3D
  Placement = pos=(-3,28,2.5) rot=(0,0,1;0rad)
  Radius = 1.5
FEATURE [Part::Sphere] Sphere042
  Angle1 = -90
  Angle2 = 90
  Angle3 = 360
  AttacherType = Attacher::AttachEngine3D
  Placement = pos=(-3,34,2.5) rot=(0,0,1;0rad)
  Radius = 1.5
FEATURE [Part::MultiFuse] Fusion034
  Shapes = -> [Box107,Box110,Box109,Box108,Box106]
FEATURE [Part::Cut] Cut029
  Base = -> Fusion034
  Tool = -> Box111
FEATURE [Part::MultiFuse] Fusion035
  Shapes = -> [Sphere039,Sphere040,Cut029]
FEATURE [Part::MultiFuse] Fusion036
  Shapes = -> [Sphere042,Sphere041]
FEATURE [Part::Cut] Cut030
  Base = -> Fusion035
  Tool = -> Fusion036
FEATURE [Part::Chamfer] Chamfer010
  Base = -> Cut030
  Edges = 4 edges r=4: [Edge31,Edge37,Edge43,Edge46]
FEATURE [Part::Box] Box112  label="Cube096"
  AttacherType = Attacher::AttachEngine3D
  Height = 7
  Length = 4
  Placement = pos=(-1,5,0) rot=(0,0,1;0rad)
  Width = 1
FEATURE [Part::Box] Box113  label="Cube097"
  AttacherType = Attacher::AttachEngine3D
  Height = 7
  Length = 4
  Placement = pos=(-1,8,0) rot=(0,0,1;0rad)
  Width = 2
FEATURE [Part::Box] Box114  label="Cube098"
  AttacherType = Attacher::AttachEngine3D
  Height = 7
  Length = 4
  Placement = pos=(-1,12,0) rot=(0,0,1;0rad)
  Width = 1
FEATURE [Part::Box] Box115  label="Cube099"
  AttacherType = Attacher::AttachEngine3D
  Height = 7
  Length = 4
  Placement = pos=(-1,24.4,0) rot=(0,0,1;0rad)
  Width = 1
FEATURE [Part::Box] Box116  label="Cube100"
  AttacherType = Attacher::AttachEngine3D
  Height = 7
  Length = 4
  Placement = pos=(-1,36.6,0) rot=(0,0,1;0rad)
  Width = 1
FEATURE [Part::Box] Box117  label="Cube101"
  AttacherType = Attacher::AttachEngine3D
  Height = 7
  Length = 4
  Placement = pos=(-1,27.4,0) rot=(0,0,1;0rad)
  Width = 7.2
FEATURE [Part::MultiFuse] Fusion037
  Shapes = -> [Box117,Box114,Box116,Box113,Box115,Box112]
FEATURE [Part::Cut] Cut031
  Base = -> Chamfer010
  Placement = pos=(-5,40,3) rot=(1,0,0;3.14159rad)
  Tool = -> Fusion037
FEATURE [Part::Box] Box118  label="Cube102"
  AttacherType = Attacher::AttachEngine3D
  Height = 10
  Length = 12
  Placement = pos=(-11,-2,-12) rot=(0,0,1;0rad)
  Width = 44
FEATURE [Part::Cut] Cut032
  Base = -> Cut031
  Placement = pos=(40,0,0) rot=(0,0,1;1.5708rad)
  Tool = -> Box118
FEATURE [Part::Box] Box119  label="Cube103"
  AttacherType = Attacher::AttachEngine3D
  Height = 7
  Length = 4
  Placement = pos=(-1,12,0) rot=(0,0,1;0rad)
  Width = 1
FEATURE [Part::Box] Box120  label="Cube104"
  AttacherType = Attacher::AttachEngine3D
  Height = 10
  Length = 13
  Placement = pos=(-10.19,0,-1.19) rot=(0,-1,0;0.785398rad)
  Width = 40
FEATURE [Part::Box] Box121  label="Cube105"
  AttacherType = Attacher::AttachEngine3D
  Height = 7
  Length = 4
  Placement = pos=(-1,27.4,0) rot=(0,0,1;0rad)
  Width = 7.2
FEATURE [Part::Box] Box122  label="Cube106"
  AttacherType = Attacher::AttachEngine3D
  Height = 7
  Length = 4
  Placement = pos=(-1,5,0) rot=(0,0,1;0rad)
  Width = 1
FEATURE [Part::Box] Box123  label="Cube107"
  AttacherType = Attacher::AttachEngine3D
  Height = 7
  Length = 10
  Placement = pos=(-10,6,0) rot=(0,0,1;0rad)
  Width = 2
FEATURE [Part::Box] Box124  label="Cube108"
  AttacherType = Attacher::AttachEngine3D
  Height = 10
  Length = 12
  Placement = pos=(-11,-2,-12) rot=(0,0,1;0rad)
  Width = 44
FEATURE [Part::Sphere] Sphere043
  Angle1 = -90
  Angle2 = 90
  Angle3 = 360
  AttacherType = Attacher::AttachEngine3D
  Placement = pos=(-3,6.5,2.5) rot=(0,0,1;0rad)
  Radius = 1.25
FEATURE [Part::Box] Box125  label="Cube109"
  AttacherType = Attacher::AttachEngine3D
  Height = 7
  Length = 10
  Placement = pos=(-10,25.4,0) rot=(0,0,1;0rad)
  Width = 2
FEATURE [Part::Box] Box126  label="Cube110"
  AttacherType = Attacher::AttachEngine3D
  Height = 7
  Length = 10
  Placement = pos=(-10,10,0) rot=(0,0,1;0rad)
  Width = 2
FEATURE [Part::Sphere] Sphere044
  Angle1 = -90
  Angle2 = 90
  Angle3 = 360
  AttacherType = Attacher::AttachEngine3D
  Placement = pos=(-3,28,2.5) rot=(0,0,1;0rad)
  Radius = 1.5
FEATURE [Part::Sphere] Sphere045
  Angle1 = -90
  Angle2 = 90
  Angle3 = 360
  AttacherType = Attacher::AttachEngine3D
  Placement = pos=(-3,11.5,2.5) rot=(0,0,1;0rad)
  Radius = 1.25
FEATURE [Part::Box] Box127  label="Cube111"
  AttacherType = Attacher::AttachEngine3D
  Height = 7
  Length = 4
  Placement = pos=(-1,36.6,0) rot=(0,0,1;0rad)
  Width = 1
FEATURE [Part::Sphere] Sphere046
  Angle1 = -90
  Angle2 = 90
  Angle3 = 360
  AttacherType = Attacher::AttachEngine3D
  Placement = pos=(-3,34,2.5) rot=(0,0,1;0rad)
  Radius = 1.5
FEATURE [Part::MultiFuse] Fusion040
  Shapes = -> [Sphere046,Sphere044]
FEATURE [Part::Box] Box128  label="Cube112"
  AttacherType = Attacher::AttachEngine3D
  Height = 7
  Length = 4
  Placement = pos=(-1,8,0) rot=(0,0,1;0rad)
  Width = 2
FEATURE [Part::Box] Box129  label="Cube113"
  AttacherType = Attacher::AttachEngine3D
  Height = 7
  Length = 10
  Placement = pos=(-10,34.6,0) rot=(0,0,1;0rad)
  Width = 2
FEATURE [Part::Box] Box130  label="Cube114"
  AttacherType = Attacher::AttachEngine3D
  Height = 7
  Length = 4
  Placement = pos=(-1,24.4,0) rot=(0,0,1;0rad)
  Width = 1
FEATURE [Part::MultiFuse] Fusion038
  Shapes = -> [Box121,Box119,Box127,Box128,Box130,Box122]
FEATURE [Part::Box] Box131  label="Cube115"
  AttacherType = Attacher::AttachEngine3D
  Height = 7
  Length = 5
  Width = 40
FEATURE [Part::MultiFuse] Fusion041
  Shapes = -> [Box131,Box123,Box126,Box125,Box129]
FEATURE [Part::Cut] Cut035
  Base = -> Fusion041
  Tool = -> Box120
FEATURE [Part::MultiFuse] Fusion039
  Shapes = -> [Sphere043,Sphere045,Cut035]
FEATURE [Part::Cut] Cut036
  Base = -> Fusion039
  Tool = -> Fusion040
FEATURE [Part::Chamfer] Chamfer011
  Base = -> Cut036
  Edges = 4 edges r=4: [Edge31,Edge37,Edge43,Edge46]
FEATURE [Part::Cut] Cut034
  Base = -> Chamfer011
  Placement = pos=(-5,40,3) rot=(1,0,0;3.14159rad)
  Tool = -> Fusion038
FEATURE [Part::Cut] Cut033
  Base = -> Cut034
  Placement = pos=(40,40,0) rot=(0,0,1;3.14159rad)
  Tool = -> Box124
FEATURE [Part::Sphere] Sphere047
  Angle1 = -90
  Angle2 = 90
  Angle3 = 360
  AttacherType = Attacher::AttachEngine3D
  Placement = pos=(-3,11.5,2.5) rot=(0,0,1;0rad)
  Radius = 1.25
FEATURE [Part::Box] Box132  label="Cube116"
  AttacherType = Attacher::AttachEngine3D
  Height = 7
  Length = 10
  Placement = pos=(-10,6,0) rot=(0,0,1;0rad)
  Width = 2
FEATURE [Part::Box] Box133  label="Cube117"
  AttacherType = Attacher::AttachEngine3D
  Height = 7
  Length = 4
  Placement = pos=(-1,8,0) rot=(0,0,1;0rad)
  Width = 2
FEATURE [Part::Box] Box134  label="Cube118"
  AttacherType = Attacher::AttachEngine3D
  Height = 7
  Length = 10
  Placement = pos=(-10,10,0) rot=(0,0,1;0rad)
  Width = 2
FEATURE [Part::Box] Box135  label="Cube119"
  AttacherType = Attacher::AttachEngine3D
  Height = 10
  Length = 12
  Placement = pos=(-11,-2,-12) rot=(0,0,1;0rad)
  Width = 44
FEATURE [Part::Box] Box136  label="Cube120"
  AttacherType = Attacher::AttachEngine3D
  Height = 7
  Length = 4
  Placement = pos=(-1,5,0) rot=(0,0,1;0rad)
  Width = 1
FEATURE [Part::Sphere] Sphere048
  Angle1 = -90
  Angle2 = 90
  Angle3 = 360
  AttacherType = Attacher::AttachEngine3D
  Placement = pos=(-3,28,2.5) rot=(0,0,1;0rad)
  Radius = 1.5
FEATURE [Part::Sphere] Sphere049
  Angle1 = -90
  Angle2 = 90
  Angle3 = 360
  AttacherType = Attacher::AttachEngine3D
  Placement = pos=(-3,6.5,2.5) rot=(0,0,1;0rad)
  Radius = 1.25
FEATURE [Part::Sphere] Sphere050
  Angle1 = -90
  Angle2 = 90
  Angle3 = 360
  AttacherType = Attacher::AttachEngine3D
  Placement = pos=(-3,34,2.5) rot=(0,0,1;0rad)
  Radius = 1.5
FEATURE [Part::Box] Box137  label="Cube121"
  AttacherType = Attacher::AttachEngine3D
  Height = 7
  Length = 4
  Placement = pos=(-1,12,0) rot=(0,0,1;0rad)
  Width = 1
FEATURE [Part::Box] Box138  label="Cube122"
  AttacherType = Attacher::AttachEngine3D
  Height = 7
  Length = 5
  Width = 40
FEATURE [Part::Box] Box139  label="Cube123"
  AttacherType = Attacher::AttachEngine3D
  Height = 7
  Length = 4
  Placement = pos=(-1,36.6,0) rot=(0,0,1;0rad)
  Width = 1
FEATURE [Part::Box] Box140  label="Cube124"
  AttacherType = Attacher::AttachEngine3D
  Height = 7
  Length = 4
  Placement = pos=(-1,24.4,0) rot=(0,0,1;0rad)
  Width = 1
FEATURE [Part::Box] Box141  label="Cube125"
  AttacherType = Attacher::AttachEngine3D
  Height = 7
  Length = 10
  Placement = pos=(-10,25.4,0) rot=(0,0,1;0rad)
  Width = 2
FEATURE [Part::Box] Box142  label="Cube126"
  AttacherType = Attacher::AttachEngine3D
  Height = 10
  Length = 13
  Placement = pos=(-10.19,0,-1.19) rot=(0,-1,0;0.785398rad)
  Width = 40
FEATURE [Part::Box] Box143  label="Cube127"
  AttacherType = Attacher::AttachEngine3D
  Height = 7
  Length = 10
  Placement = pos=(-10,34.6,0) rot=(0,0,1;0rad)
  Width = 2
FEATURE [Part::MultiFuse] Fusion044
  Shapes = -> [Box138,Box132,Box134,Box141,Box143]
FEATURE [Part::Cut] Cut037
  Base = -> Fusion044
  Tool = -> Box142
FEATURE [Part::MultiFuse] Fusion042
  Shapes = -> [Sphere049,Sphere047,Cut037]
FEATURE [Part::MultiFuse] Fusion045
  Shapes = -> [Sphere050,Sphere048]
FEATURE [Part::Cut] Cut038
  Base = -> Fusion042
  Tool = -> Fusion045
FEATURE [Part::Chamfer] Chamfer012
  Base = -> Cut038
  Edges = 4 edges r=4: [Edge31,Edge37,Edge43,Edge46]
FEATURE [Part::Box] Box144  label="Cube128"
  AttacherType = Attacher::AttachEngine3D
  Height = 7
  Length = 4
  Placement = pos=(-1,27.4,0) rot=(0,0,1;0rad)
  Width = 7.2
FEATURE [Part::MultiFuse] Fusion043
  Shapes = -> [Box144,Box137,Box139,Box133,Box140,Box136]
FEATURE [Part::Cut] Cut040
  Base = -> Chamfer012
  Placement = pos=(-5,40,3) rot=(1,0,0;3.14159rad)
  Tool = -> Fusion043
FEATURE [Part::Cut] Cut039
  Base = -> Cut040
  Placement = pos=(0,40,0) rot=(0,0,-1;1.5708rad)
  Tool = -> Box135
FEATURE [Part::MultiFuse] Fusion048
  Shapes = -> [Box089,Box091,Box090,Box092]
FEATURE [Part::Box] Box145  label="Cube129"
  AttacherType = Attacher::AttachEngine3D
  Height = 15
  Length = 19.5
  Placement = pos=(-9.75,-9.75,-14) rot=(0,0,1;0rad)
  Width = 19.5
FEATURE [Part::Box] Box146  label="Cube130"
  AttacherType = Attacher::AttachEngine3D
  Height = 15
  Length = 19.5
  Placement = pos=(-9.75,-9.75,-3) rot=(0,0,1;0rad)
  Width = 19.5
FEATURE [Part::Chamfer] Chamfer013  label="Octagon"
  Base = -> Box146
  Edges = 4 edges r=4: [Edge1,Edge3,Edge5,Edge7]
FEATURE [Part::Box] Box147  label="Cube131"
  AttacherType = Attacher::AttachEngine3D
  Height = 10
  Length = 24
  Placement = pos=(-12,-12,2.1) rot=(0,0,1;0rad)
  Width = 24
FEATURE [Part::Box] Box148  label="Cube132"
  AttacherType = Attacher::AttachEngine3D
  Height = 14
  Length = 20
  Placement = pos=(-10,-10,0) rot=(0,0,1;0rad)
  Width = 20
FEATURE [Part::Cut] Cut043
  Base = -> Box147
  Tool = -> Box148
FEATURE [Part::Chamfer] Chamfer014  label="Glue Channel"
  Base = -> Cut043
  Edges = 8 edges r=0.95: [Edge4,Edge5,Edge14,Edge16,Edge17,Edge18,Edge19,Edge20]
FEATURE [Part::Cut] Cut047
  Base = -> Cut003
  Tool = -> Chamfer007
FEATURE [Part::Cylinder] Cylinder024
  Angle = 360
  AttacherType = Attacher::AttachEngine3D
  Height = 10
  Placement = pos=(-15,-15,-5) rot=(0,0,1;0rad)
  Radius = 1.7
FEATURE [Part::Cylinder] Cylinder025
  Angle = 360
  AttacherType = Attacher::AttachEngine3D
  Height = 10
  Placement = pos=(15,0,-5) rot=(0,0,1;0rad)
  Radius = 1.7
FEATURE [Part::Cylinder] Cylinder026
  Angle = 360
  AttacherType = Attacher::AttachEngine3D
  Height = 10
  Placement = pos=(-15,15,-5) rot=(0,0,1;0rad)
  Radius = 1.7
FEATURE [Part::MultiFuse] Fusion052  label="Screw Holes to remove ball mags"
  Shapes = -> [Cylinder024,Cylinder025,Cylinder026]
FEATURE [Drawing::FeatureViewAnnotation] Annotation
  Font = Sans
  Rotation = 0
  Scale = 7
  Text = 0.4Added in Holes to Mag plate for removal of magnet
  ViewResult = <g transform="translate(14,23) rotate(0)">\n<text id="Annotation"\n font-family="Sans"\n font-size="7"\n fill="#000000">\n<tspan x="0" dy="1em">0.4Added in Holes to Mag plate for removal of magnet</tspan>\n</text>\n</g>
  Visible = false
  X = 14
  Y = 23
FEATURE [Part::Box] Box149  label="Re-level Edge Clip Block001"
  AttacherType = Attacher::AttachEngine3D
  Height = 10
  Length = 12
  Placement = pos=(-21.5,-2,-7) rot=(0,0,1;0rad)
  Width = 44
FEATURE [Part::Fuse] Fusion  label="Bumps"
  Base = -> Sphere008
  Tool = -> Sphere009
FEATURE [Part::Fuse] Fusion053  label="Holes"
  Base = -> Sphere010
  Tool = -> Sphere011
FEATURE [Part::MultiFuse] Fusion054
  Shapes = -> [Box001,Box002,Box003,Box004,Box005]
FEATURE [Part::Fuse] Fusion055
  Base = -> Fusion
  Tool = -> Fusion054
FEATURE [Part::Cut] Cut
  Base = -> Fusion055
  Tool = -> Fusion053
FEATURE [Part::Cut] Cut056
  Base = -> Cut
  Tool = -> Fusion003
FEATURE [Part::Cut] Cut057
  Base = -> Cut056
  Tool = -> Box013
FEATURE [Part::Cut] Cut058
  Base = -> Cut057
  Tool = -> Box149
FEATURE [Part::Cut] Cut059  label="Edge Clips Master"
  Base = -> Cut058
  Placement = pos=(-20,-20,0) rot=(0,0,1;0rad)
  Tool = -> Box006
FEATURE [Part::Box] Box150  label="Cube133"
  AttacherType = Attacher::AttachEngine3D
  Height = 7
  Length = 5
  Placement = pos=(-5,0,-2) rot=(0,0,1;0rad)
  Width = 40
FEATURE [Part::Box] Box151  label="Cube134"
  AttacherType = Attacher::AttachEngine3D
  Height = 7
  Length = 10
  Placement = pos=(-15,6,-2) rot=(0,0,1;0rad)
  Width = 2
FEATURE [Part::Box] Box152  label="Cube135"
  AttacherType = Attacher::AttachEngine3D
  Height = 7
  Length = 10
  Placement = pos=(-15,10,-2) rot=(0,0,1;0rad)
  Width = 2
FEATURE [Part::Box] Box153  label="Cube136"
  AttacherType = Attacher::AttachEngine3D
  Height = 7
  Length = 10
  Placement = pos=(-15,25.4,-2) rot=(0,0,1;0rad)
  Width = 2
FEATURE [Part::Box] Box154  label="Cube137"
  AttacherType = Attacher::AttachEngine3D
  Height = 7
  Length = 10
  Placement = pos=(-15,34.6,-2) rot=(0,0,1;0rad)
  Width = 2
FEATURE [Part::Sphere] Sphere051
  Angle1 = -90
  Angle2 = 90
  Angle3 = 360
  AttacherType = Attacher::AttachEngine3D
  Placement = pos=(-7.5,6.5,0.5) rot=(0,0,1;0rad)
  Radius = 1.25
FEATURE [Part::Box] Box155  label="Chamfer Cube001"
  AttacherType = Attacher::AttachEngine3D
  Height = 10
  Length = 13
  Placement = pos=(-11.69,0,-1.19) rot=(0,-1,0;0.785398rad)
  Width = 40
FEATURE [Part::Sphere] Sphere052
  Angle1 = -90
  Angle2 = 90
  Angle3 = 360
  AttacherType = Attacher::AttachEngine3D
  Placement = pos=(-7.5,11.5,0.5) rot=(0,0,1;0rad)
  Radius = 1.25
FEATURE [Part::Sphere] Sphere053
  Angle1 = -90
  Angle2 = 90
  Angle3 = 360
  AttacherType = Attacher::AttachEngine3D
  Placement = pos=(-7.5,28,0.5) rot=(0,0,1;0rad)
  Radius = 1.5
FEATURE [Part::Sphere] Sphere054
  Angle1 = -90
  Angle2 = 90
  Angle3 = 360
  AttacherType = Attacher::AttachEngine3D
  Placement = pos=(-7.5,34,0.5) rot=(0,0,1;0rad)
  Radius = 1.5
FEATURE [Part::Box] Box156  label="Cube138"
  AttacherType = Attacher::AttachEngine3D
  Height = 7
  Length = 4
  Placement = pos=(-6,5,-2) rot=(0,0,1;0rad)
  Width = 1
FEATURE [Part::Box] Box157  label="Cube139"
  AttacherType = Attacher::AttachEngine3D
  Height = 7
  Length = 4
  Placement = pos=(-6,8,-2) rot=(0,0,1;0rad)
  Width = 2
FEATURE [Part::Box] Box158  label="Cube140"
  AttacherType = Attacher::AttachEngine3D
  Height = 7
  Length = 4
  Placement = pos=(-6,12,-2) rot=(0,0,1;0rad)
  Width = 1
FEATURE [Part::Box] Box159  label="Cube141"
  AttacherType = Attacher::AttachEngine3D
  Height = 7
  Length = 4
  Placement = pos=(-6,24.4,-2) rot=(0,0,1;0rad)
  Width = 1
FEATURE [Part::Box] Box160  label="Cube142"
  AttacherType = Attacher::AttachEngine3D
  Height = 7
  Length = 4
  Placement = pos=(-6,36.6,-2) rot=(0,0,1;0rad)
  Width = 1
FEATURE [Part::Box] Box161  label="Cube143"
  AttacherType = Attacher::AttachEngine3D
  Height = 7
  Length = 4
  Placement = pos=(-6,27.4,-2) rot=(0,0,1;0rad)
  Width = 7.2
FEATURE [Part::MultiFuse] Fusion056  label="Extra Holes for Clips001"
  Shapes = -> [Box161,Box158,Box160,Box157,Box159,Box156]
FEATURE [Part::Box] Box162  label="Re-level Edge Clip Block002"
  AttacherType = Attacher::AttachEngine3D
  Height = 10
  Length = 20
  Placement = pos=(-19,-2,3) rot=(0,0,1;0rad)
  Width = 44
FEATURE [Part::Box] Box163  label="Re-level Edge Clip Block003"
  AttacherType = Attacher::AttachEngine3D
  Height = 10
  Length = 12
  Placement = pos=(-21.5,-2,-7) rot=(0,0,1;0rad)
  Width = 44
FEATURE [Part::Fuse] Fusion057  label="Bumps001"
  Base = -> Sphere051
  Tool = -> Sphere052
FEATURE [Part::Fuse] Fusion058  label="Holes001"
  Base = -> Sphere053
  Tool = -> Sphere054
FEATURE [Part::MultiFuse] Fusion059
  Shapes = -> [Box150,Box151,Box152,Box153,Box154]
FEATURE [Part::Fuse] Fusion060
  Base = -> Fusion057
  Tool = -> Fusion059
FEATURE [Part::Cut] Cut060
  Base = -> Fusion060
  Tool = -> Fusion058
FEATURE [Part::Cut] Cut061
  Base = -> Cut060
  Tool = -> Fusion056
FEATURE [Part::Cut] Cut062
  Base = -> Cut061
  Tool = -> Box162
FEATURE [Part::Cut] Cut063
  Base = -> Cut062
  Tool = -> Box163
FEATURE [Part::Cut] Cut064  label="Copy Edge Clip"
  Base = -> Cut063
  Placement = pos=(-27,20,-7) rot=(0.707107,0,-0.707107;3.14159rad)
  Tool = -> Box155
FEATURE [Part::Box] Box164  label="Cube144"
  AttacherType = Attacher::AttachEngine3D
  Height = 7
  Length = 5
  Placement = pos=(-5,0,-2) rot=(0,0,1;0rad)
  Width = 40
FEATURE [Part::Box] Box165  label="Cube145"
  AttacherType = Attacher::AttachEngine3D
  Height = 7
  Length = 10
  Placement = pos=(-15,6,-2) rot=(0,0,1;0rad)
  Width = 2
FEATURE [Part::Box] Box166  label="Cube146"
  AttacherType = Attacher::AttachEngine3D
  Height = 7
  Length = 10
  Placement = pos=(-15,10,-2) rot=(0,0,1;0rad)
  Width = 2
FEATURE [Part::Box] Box167  label="Cube147"
  AttacherType = Attacher::AttachEngine3D
  Height = 7
  Length = 10
  Placement = pos=(-15,25.4,-2) rot=(0,0,1;0rad)
  Width = 2
FEATURE [Part::Box] Box168  label="Cube148"
  AttacherType = Attacher::AttachEngine3D
  Height = 7
  Length = 10
  Placement = pos=(-15,34.6,-2) rot=(0,0,1;0rad)
  Width = 2
FEATURE [Part::Sphere] Sphere055
  Angle1 = -90
  Angle2 = 90
  Angle3 = 360
  AttacherType = Attacher::AttachEngine3D
  Placement = pos=(-7.5,6.5,0.5) rot=(0,0,1;0rad)
  Radius = 1.25
FEATURE [Part::Box] Box169  label="Chamfer Cube002"
  AttacherType = Attacher::AttachEngine3D
  Height = 10
  Length = 13
  Placement = pos=(-11.69,0,-1.19) rot=(0,-1,0;0.785398rad)
  Width = 40
FEATURE [Part::Sphere] Sphere056
  Angle1 = -90
  Angle2 = 90
  Angle3 = 360
  AttacherType = Attacher::AttachEngine3D
  Placement = pos=(-7.5,11.5,0.5) rot=(0,0,1;0rad)
  Radius = 1.25
FEATURE [Part::Sphere] Sphere057
  Angle1 = -90
  Angle2 = 90
  Angle3 = 360
  AttacherType = Attacher::AttachEngine3D
  Placement = pos=(-7.5,28,0.5) rot=(0,0,1;0rad)
  Radius = 1.5
FEATURE [Part::Sphere] Sphere058
  Angle1 = -90
  Angle2 = 90
  Angle3 = 360
  AttacherType = Attacher::AttachEngine3D
  Placement = pos=(-7.5,34,0.5) rot=(0,0,1;0rad)
  Radius = 1.5
FEATURE [Part::Box] Box170  label="Cube149"
  AttacherType = Attacher::AttachEngine3D
  Height = 7
  Length = 4
  Placement = pos=(-6,5,-2) rot=(0,0,1;0rad)
  Width = 1
FEATURE [Part::Box] Box171  label="Cube150"
  AttacherType = Attacher::AttachEngine3D
  Height = 7
  Length = 4
  Placement = pos=(-6,8,-2) rot=(0,0,1;0rad)
  Width = 2
FEATURE [Part::Box] Box172  label="Cube151"
  AttacherType = Attacher::AttachEngine3D
  Height = 7
  Length = 4
  Placement = pos=(-6,12,-2) rot=(0,0,1;0rad)
  Width = 1
FEATURE [Part::Box] Box173  label="Cube152"
  AttacherType = Attacher::AttachEngine3D
  Height = 7
  Length = 4
  Placement = pos=(-6,24.4,-2) rot=(0,0,1;0rad)
  Width = 1
FEATURE [Part::Box] Box174  label="Cube153"
  AttacherType = Attacher::AttachEngine3D
  Height = 7
  Length = 4
  Placement = pos=(-6,36.6,-2) rot=(0,0,1;0rad)
  Width = 1
FEATURE [Part::Box] Box175  label="Cube154"
  AttacherType = Attacher::AttachEngine3D
  Height = 7
  Length = 4
  Placement = pos=(-6,27.4,-2) rot=(0,0,1;0rad)
  Width = 7.2
FEATURE [Part::MultiFuse] Fusion061  label="Extra Holes for Clips002"
  Shapes = -> [Box175,Box172,Box174,Box171,Box173,Box170]
FEATURE [Part::Box] Box176  label="Re-level Edge Clip Block004"
  AttacherType = Attacher::AttachEngine3D
  Height = 10
  Length = 20
  Placement = pos=(-19,-2,3) rot=(0,0,1;0rad)
  Width = 44
FEATURE [Part::Box] Box177  label="Re-level Edge Clip Block005"
  AttacherType = Attacher::AttachEngine3D
  Height = 10
  Length = 12
  Placement = pos=(-21.5,-2,-7) rot=(0,0,1;0rad)
  Width = 44
FEATURE [Part::Fuse] Fusion062  label="Bumps002"
  Base = -> Sphere055
  Tool = -> Sphere056
FEATURE [Part::Fuse] Fusion063  label="Holes002"
  Base = -> Sphere057
  Tool = -> Sphere058
FEATURE [Part::MultiFuse] Fusion064
  Shapes = -> [Box164,Box165,Box166,Box167,Box168]
FEATURE [Part::Fuse] Fusion065
  Base = -> Fusion062
  Tool = -> Fusion064
FEATURE [Part::Cut] Cut065
  Base = -> Fusion065
  Tool = -> Fusion063
FEATURE [Part::Cut] Cut066
  Base = -> Cut065
  Tool = -> Fusion061
FEATURE [Part::Cut] Cut067
  Base = -> Cut066
  Tool = -> Box176
FEATURE [Part::Cut] Cut068
  Base = -> Cut067
  Tool = -> Box177
FEATURE [Part::Cut] Cut069  label="Edge Clips001"
  Base = -> Cut068
  Placement = pos=(20,-20,0) rot=(0,0,1;1.5708rad)
  Tool = -> Box169
FEATURE [Part::Box] Box178  label="Cube155"
  AttacherType = Attacher::AttachEngine3D
  Height = 7
  Length = 5
  Placement = pos=(-5,0,-2) rot=(0,0,1;0rad)
  Width = 40
FEATURE [Part::Box] Box179  label="Cube156"
  AttacherType = Attacher::AttachEngine3D
  Height = 7
  Length = 10
  Placement = pos=(-15,10,-2) rot=(0,0,1;0rad)
  Width = 2
FEATURE [Part::Box] Box180  label="Re-level Edge Clip Block006"
  AttacherType = Attacher::AttachEngine3D
  Height = 10
  Length = 20
  Placement = pos=(-19,-2,3) rot=(0,0,1;0rad)
  Width = 44
FEATURE [Part::Box] Box181  label="Cube157"
  AttacherType = Attacher::AttachEngine3D
  Height = 7
  Length = 4
  Placement = pos=(-6,27.4,-2) rot=(0,0,1;0rad)
  Width = 7.2
FEATURE [Part::Box] Box182  label="Cube158"
  AttacherType = Attacher::AttachEngine3D
  Height = 7
  Length = 4
  Placement = pos=(-6,12,-2) rot=(0,0,1;0rad)
  Width = 1
FEATURE [Part::Sphere] Sphere059
  Angle1 = -90
  Angle2 = 90
  Angle3 = 360
  AttacherType = Attacher::AttachEngine3D
  Placement = pos=(-7.5,6.5,0.5) rot=(0,0,1;0rad)
  Radius = 1.25
FEATURE [Part::Box] Box183  label="Cube159"
  AttacherType = Attacher::AttachEngine3D
  Height = 7
  Length = 10
  Placement = pos=(-15,25.4,-2) rot=(0,0,1;0rad)
  Width = 2
FEATURE [Part::Box] Box184  label="Cube160"
  AttacherType = Attacher::AttachEngine3D
  Height = 7
  Length = 4
  Placement = pos=(-6,36.6,-2) rot=(0,0,1;0rad)
  Width = 1
FEATURE [Part::Sphere] Sphere060
  Angle1 = -90
  Angle2 = 90
  Angle3 = 360
  AttacherType = Attacher::AttachEngine3D
  Placement = pos=(-7.5,34,0.5) rot=(0,0,1;0rad)
  Radius = 1.5
FEATURE [Part::Box] Box185  label="Cube161"
  AttacherType = Attacher::AttachEngine3D
  Height = 7
  Length = 4
  Placement = pos=(-6,24.4,-2) rot=(0,0,1;0rad)
  Width = 1
FEATURE [Part::Box] Box186  label="Cube162"
  AttacherType = Attacher::AttachEngine3D
  Height = 7
  Length = 4
  Placement = pos=(-6,8,-2) rot=(0,0,1;0rad)
  Width = 2
FEATURE [Part::Box] Box187  label="Re-level Edge Clip Block007"
  AttacherType = Attacher::AttachEngine3D
  Height = 10
  Length = 12
  Placement = pos=(-21.5,-2,-7) rot=(0,0,1;0rad)
  Width = 44
FEATURE [Part::Sphere] Sphere061
  Angle1 = -90
  Angle2 = 90
  Angle3 = 360
  AttacherType = Attacher::AttachEngine3D
  Placement = pos=(-7.5,11.5,0.5) rot=(0,0,1;0rad)
  Radius = 1.25
FEATURE [Part::Sphere] Sphere062
  Angle1 = -90
  Angle2 = 90
  Angle3 = 360
  AttacherType = Attacher::AttachEngine3D
  Placement = pos=(-7.5,28,0.5) rot=(0,0,1;0rad)
  Radius = 1.5
FEATURE [Part::Fuse] Fusion066  label="Holes003"
  Base = -> Sphere062
  Tool = -> Sphere060
FEATURE [Part::Box] Box188  label="Cube163"
  AttacherType = Attacher::AttachEngine3D
  Height = 7
  Length = 10
  Placement = pos=(-15,34.6,-2) rot=(0,0,1;0rad)
  Width = 2
FEATURE [Part::Box] Box189  label="Cube164"
  AttacherType = Attacher::AttachEngine3D
  Height = 7
  Length = 4
  Placement = pos=(-6,5,-2) rot=(0,0,1;0rad)
  Width = 1
FEATURE [Part::MultiFuse] Fusion067  label="Extra Holes for Clips003"
  Shapes = -> [Box181,Box182,Box184,Box186,Box185,Box189]
FEATURE [Part::Box] Box190  label="Cube165"
  AttacherType = Attacher::AttachEngine3D
  Height = 7
  Length = 10
  Placement = pos=(-15,6,-2) rot=(0,0,1;0rad)
  Width = 2
FEATURE [Part::MultiFuse] Fusion069
  Shapes = -> [Box178,Box190,Box179,Box183,Box188]
FEATURE [Part::Fuse] Fusion070  label="Bumps003"
  Base = -> Sphere059
  Tool = -> Sphere061
FEATURE [Part::Fuse] Fusion068
  Base = -> Fusion070
  Tool = -> Fusion069
FEATURE [Part::Cut] Cut073
  Base = -> Fusion068
  Tool = -> Fusion066
FEATURE [Part::Cut] Cut070
  Base = -> Cut073
  Tool = -> Fusion067
FEATURE [Part::Cut] Cut071
  Base = -> Cut070
  Tool = -> Box180
FEATURE [Part::Cut] Cut072
  Base = -> Cut071
  Tool = -> Box187
FEATURE [Part::Box] Box191  label="Chamfer Cube003"
  AttacherType = Attacher::AttachEngine3D
  Height = 10
  Length = 13
  Placement = pos=(-11.69,0,-1.19) rot=(0,-1,0;0.785398rad)
  Width = 40
FEATURE [Part::Cut] Cut074  label="Edge Clips002"
  Base = -> Cut072
  Placement = pos=(20,20,0) rot=(0,0,1;3.14159rad)
  Tool = -> Box191
FEATURE [Part::Box] Box192  label="Cube166"
  AttacherType = Attacher::AttachEngine3D
  Height = 7
  Length = 10
  Placement = pos=(-15,6,-2) rot=(0,0,1;0rad)
  Width = 2
FEATURE [Part::Box] Box193  label="Chamfer Cube004"
  AttacherType = Attacher::AttachEngine3D
  Height = 10
  Length = 13
  Placement = pos=(-11.69,0,-1.19) rot=(0,-1,0;0.785398rad)
  Width = 40
FEATURE [Part::Box] Box194  label="Re-level Edge Clip Block008"
  AttacherType = Attacher::AttachEngine3D
  Height = 10
  Length = 20
  Placement = pos=(-19,-2,3) rot=(0,0,1;0rad)
  Width = 44
FEATURE [Part::Box] Box195  label="Cube167"
  AttacherType = Attacher::AttachEngine3D
  Height = 7
  Length = 10
  Placement = pos=(-15,10,-2) rot=(0,0,1;0rad)
  Width = 2
FEATURE [Part::Box] Box196  label="Cube168"
  AttacherType = Attacher::AttachEngine3D
  Height = 7
  Length = 5
  Placement = pos=(-5,0,-2) rot=(0,0,1;0rad)
  Width = 40
FEATURE [Part::Box] Box197  label="Cube169"
  AttacherType = Attacher::AttachEngine3D
  Height = 7
  Length = 4
  Placement = pos=(-6,5,-2) rot=(0,0,1;0rad)
  Width = 1
FEATURE [Part::Box] Box198  label="Cube170"
  AttacherType = Attacher::AttachEngine3D
  Height = 7
  Length = 4
  Placement = pos=(-6,12,-2) rot=(0,0,1;0rad)
  Width = 1
FEATURE [Part::Box] Box199  label="Cube171"
  AttacherType = Attacher::AttachEngine3D
  Height = 7
  Length = 4
  Placement = pos=(-6,27.4,-2) rot=(0,0,1;0rad)
  Width = 7.2
FEATURE [Part::Box] Box200  label="Cube172"
  AttacherType = Attacher::AttachEngine3D
  Height = 7
  Length = 4
  Placement = pos=(-6,24.4,-2) rot=(0,0,1;0rad)
  Width = 1
FEATURE [Part::Sphere] Sphere063
  Angle1 = -90
  Angle2 = 90
  Angle3 = 360
  AttacherType = Attacher::AttachEngine3D
  Placement = pos=(-7.5,28,0.5) rot=(0,0,1;0rad)
  Radius = 1.5
FEATURE [Part::Sphere] Sphere064
  Angle1 = -90
  Angle2 = 90
  Angle3 = 360
  AttacherType = Attacher::AttachEngine3D
  Placement = pos=(-7.5,11.5,0.5) rot=(0,0,1;0rad)
  Radius = 1.25
FEATURE [Part::Box] Box201  label="Cube173"
  AttacherType = Attacher::AttachEngine3D
  Height = 7
  Length = 4
  Placement = pos=(-6,8,-2) rot=(0,0,1;0rad)
  Width = 2
FEATURE [Part::Box] Box202  label="Cube174"
  AttacherType = Attacher::AttachEngine3D
  Height = 7
  Length = 10
  Placement = pos=(-15,25.4,-2) rot=(0,0,1;0rad)
  Width = 2
FEATURE [Part::Sphere] Sphere065
  Angle1 = -90
  Angle2 = 90
  Angle3 = 360
  AttacherType = Attacher::AttachEngine3D
  Placement = pos=(-7.5,6.5,0.5) rot=(0,0,1;0rad)
  Radius = 1.25
FEATURE [Part::Fuse] Fusion073  label="Bumps004"
  Base = -> Sphere065
  Tool = -> Sphere064
FEATURE [Part::Sphere] Sphere066
  Angle1 = -90
  Angle2 = 90
  Angle3 = 360
  AttacherType = Attacher::AttachEngine3D
  Placement = pos=(-7.5,34,0.5) rot=(0,0,1;0rad)
  Radius = 1.5
FEATURE [Part::Fuse] Fusion071  label="Holes004"
  Base = -> Sphere063
  Tool = -> Sphere066
FEATURE [Part::Box] Box203  label="Re-level Edge Clip Block009"
  AttacherType = Attacher::AttachEngine3D
  Height = 10
  Length = 12
  Placement = pos=(-21.5,-2,-7) rot=(0,0,1;0rad)
  Width = 44
FEATURE [Part::Box] Box204  label="Cube175"
  AttacherType = Attacher::AttachEngine3D
  Height = 7
  Length = 4
  Placement = pos=(-6,36.6,-2) rot=(0,0,1;0rad)
  Width = 1
FEATURE [Part::MultiFuse] Fusion074  label="Extra Holes for Clips004"
  Shapes = -> [Box199,Box198,Box204,Box201,Box200,Box197]
FEATURE [Part::Box] Box205  label="Cube176"
  AttacherType = Attacher::AttachEngine3D
  Height = 7
  Length = 10
  Placement = pos=(-15,34.6,-2) rot=(0,0,1;0rad)
  Width = 2
FEATURE [Part::MultiFuse] Fusion072
  Shapes = -> [Box196,Box192,Box195,Box202,Box205]
FEATURE [Part::Fuse] Fusion075
  Base = -> Fusion073
  Tool = -> Fusion072
FEATURE [Part::Cut] Cut075
  Base = -> Fusion075
  Tool = -> Fusion071
FEATURE [Part::Cut] Cut076
  Base = -> Cut075
  Tool = -> Fusion074
FEATURE [Part::Cut] Cut078
  Base = -> Cut076
  Tool = -> Box194
FEATURE [Part::Cut] Cut077
  Base = -> Cut078
  Tool = -> Box203
FEATURE [Part::Cut] Cut079  label="Edge Clips003"
  Base = -> Cut077
  Placement = pos=(-20,20,0) rot=(0,0,-1;1.5708rad)
  Tool = -> Box193
FEATURE [Part::MultiFuse] Fusion076  label="Edge Clips Fusion"
  Shapes = -> [Cut059,Cut069,Cut074,Cut079]
FEATURE [Part::Box] Box206  label="Cube177"
  AttacherType = Attacher::AttachEngine3D
  Height = 10
  Length = 10
  Placement = pos=(26,4,1) rot=(0.442189,-0.287968,0.849437;1.66134rad)
  Width = 15
FEATURE [Part::Box] Box207  label="Cube178"
  AttacherType = Attacher::AttachEngine3D
  Height = 10
  Length = 10
  Placement = pos=(-4,26,1) rot=(0.381439,0.080566,0.920876;3.07487rad)
  Width = 15
FEATURE [Part::Box] Box208  label="Cube179"
  AttacherType = Attacher::AttachEngine3D
  Height = 10
  Length = 10
  Placement = pos=(-26,-4,1) rot=(-0.273007,-0.419215,-0.865867;1.78566rad)
  Width = 15
FEATURE [Part::MultiFuse] Fusion078  label="Glue Dents"
  Shapes = -> [Box086,Box208,Box207,Box206]
FEATURE [Part::Box] Box209  label="Cube180"
  AttacherType = Attacher::AttachEngine3D
  Height = 7
  Length = 5
  Placement = pos=(-5,0,-2) rot=(0,0,1;0rad)
  Width = 40
FEATURE [Part::Box] Box210  label="Cube181"
  AttacherType = Attacher::AttachEngine3D
  Height = 7
  Length = 10
  Placement = pos=(-15,6,-2) rot=(0,0,1;0rad)
  Width = 2
FEATURE [Part::Box] Box211  label="Cube182"
  AttacherType = Attacher::AttachEngine3D
  Height = 7
  Length = 10
  Placement = pos=(-15,10,-2) rot=(0,0,1;0rad)
  Width = 2
FEATURE [Part::Box] Box212  label="Cube183"
  AttacherType = Attacher::AttachEngine3D
  Height = 7
  Length = 10
  Placement = pos=(-15,25.4,-2) rot=(0,0,1;0rad)
  Width = 2
FEATURE [Part::Box] Box213  label="Cube184"
  AttacherType = Attacher::AttachEngine3D
  Height = 7
  Length = 10
  Placement = pos=(-15,34.6,-2) rot=(0,0,1;0rad)
  Width = 2
FEATURE [Part::Sphere] Sphere067
  Angle1 = -90
  Angle2 = 90
  Angle3 = 360
  AttacherType = Attacher::AttachEngine3D
  Placement = pos=(-7.5,6.5,0.5) rot=(0,0,1;0rad)
  Radius = 1.25
FEATURE [Part::Box] Box214  label="Chamfer Cube005"
  AttacherType = Attacher::AttachEngine3D
  Height = 10
  Length = 13
  Placement = pos=(-11.69,0,-1.19) rot=(0,-1,0;0.785398rad)
  Width = 40
FEATURE [Part::Sphere] Sphere068
  Angle1 = -90
  Angle2 = 90
  Angle3 = 360
  AttacherType = Attacher::AttachEngine3D
  Placement = pos=(-7.5,11.5,0.5) rot=(0,0,1;0rad)
  Radius = 1.25
FEATURE [Part::Sphere] Sphere069
  Angle1 = -90
  Angle2 = 90
  Angle3 = 360
  AttacherType = Attacher::AttachEngine3D
  Placement = pos=(-7.5,28,0.5) rot=(0,0,1;0rad)
  Radius = 1.5
FEATURE [Part::Sphere] Sphere070
  Angle1 = -90
  Angle2 = 90
  Angle3 = 360
  AttacherType = Attacher::AttachEngine3D
  Placement = pos=(-7.5,34,0.5) rot=(0,0,1;0rad)
  Radius = 1.5
FEATURE [Part::Box] Box215  label="Cube185"
  AttacherType = Attacher::AttachEngine3D
  Height = 7
  Length = 4
  Placement = pos=(-6,5,-2) rot=(0,0,1;0rad)
  Width = 1
FEATURE [Part::Box] Box216  label="Cube186"
  AttacherType = Attacher::AttachEngine3D
  Height = 7
  Length = 4
  Placement = pos=(-6,8,-2) rot=(0,0,1;0rad)
  Width = 2
FEATURE [Part::Box] Box217  label="Cube187"
  AttacherType = Attacher::AttachEngine3D
  Height = 7
  Length = 4
  Placement = pos=(-6,12,-2) rot=(0,0,1;0rad)
  Width = 1
FEATURE [Part::Box] Box218  label="Cube188"
  AttacherType = Attacher::AttachEngine3D
  Height = 7
  Length = 4
  Placement = pos=(-6,24.4,-2) rot=(0,0,1;0rad)
  Width = 1
FEATURE [Part::Box] Box219  label="Cube189"
  AttacherType = Attacher::AttachEngine3D
  Height = 7
  Length = 4
  Placement = pos=(-6,36.6,-2) rot=(0,0,1;0rad)
  Width = 1
FEATURE [Part::Box] Box220  label="Cube190"
  AttacherType = Attacher::AttachEngine3D
  Height = 7
  Length = 4
  Placement = pos=(-6,27.4,-2) rot=(0,0,1;0rad)
  Width = 7.2
FEATURE [Part::MultiFuse] Fusion079  label="Extra Holes for Clips005"
  Shapes = -> [Box220,Box217,Box219,Box216,Box218,Box215]
FEATURE [Part::Box] Box221  label="Re-level Edge Clip Block010"
  AttacherType = Attacher::AttachEngine3D
  Height = 10
  Length = 20
  Placement = pos=(-19,-2,3) rot=(0,0,1;0rad)
  Width = 44
FEATURE [Part::Box] Box222  label="Re-level Edge Clip Block011"
  AttacherType = Attacher::AttachEngine3D
  Height = 10
  Length = 12
  Placement = pos=(-21.5,-2,-7) rot=(0,0,1;0rad)
  Width = 44
FEATURE [Part::Fuse] Fusion080  label="Bumps005"
  Base = -> Sphere067
  Tool = -> Sphere068
FEATURE [Part::Fuse] Fusion081  label="Holes005"
  Base = -> Sphere069
  Tool = -> Sphere070
FEATURE [Part::MultiFuse] Fusion082
  Shapes = -> [Box209,Box210,Box211,Box212,Box213]
FEATURE [Part::Fuse] Fusion083
  Base = -> Fusion080
  Tool = -> Fusion082
FEATURE [Part::Cut] Cut082
  Base = -> Fusion083
  Tool = -> Fusion081
FEATURE [Part::Cut] Cut083
  Base = -> Cut082
  Tool = -> Fusion079
FEATURE [Part::Cut] Cut084
  Base = -> Cut083
  Tool = -> Box221
FEATURE [Part::Cut] Cut085
  Base = -> Cut084
  Tool = -> Box222
FEATURE [Part::Cut] Cut086  label="Edge Clips Master001"
  Base = -> Cut085
  Placement = pos=(-20,-20,0) rot=(0,0,1;0rad)
  Tool = -> Box214
FEATURE [Part::Box] Box223  label="Cube191"
  AttacherType = Attacher::AttachEngine3D
  Height = 7
  Length = 5
  Placement = pos=(-5,0,-2) rot=(0,0,1;0rad)
  Width = 40
FEATURE [Part::Box] Box224  label="Cube192"
  AttacherType = Attacher::AttachEngine3D
  Height = 7
  Length = 4
  Placement = pos=(-6,8,-2) rot=(0,0,1;0rad)
  Width = 2
FEATURE [Part::Box] Box225  label="Chamfer Cube006"
  AttacherType = Attacher::AttachEngine3D
  Height = 10
  Length = 13
  Placement = pos=(-11.69,0,-1.19) rot=(0,-1,0;0.785398rad)
  Width = 40
FEATURE [Part::Box] Box226  label="Cube193"
  AttacherType = Attacher::AttachEngine3D
  Height = 7
  Length = 10
  Placement = pos=(-15,6,-2) rot=(0,0,1;0rad)
  Width = 2
FEATURE [Part::Sphere] Sphere071
  Angle1 = -90
  Angle2 = 90
  Angle3 = 360
  AttacherType = Attacher::AttachEngine3D
  Placement = pos=(-7.5,11.5,0.5) rot=(0,0,1;0rad)
  Radius = 1.25
FEATURE [Part::Box] Box227  label="Cube194"
  AttacherType = Attacher::AttachEngine3D
  Height = 7
  Length = 4
  Placement = pos=(-6,27.4,-2) rot=(0,0,1;0rad)
  Width = 7.2
FEATURE [Part::Box] Box228  label="Cube195"
  AttacherType = Attacher::AttachEngine3D
  Height = 7
  Length = 4
  Placement = pos=(-6,12,-2) rot=(0,0,1;0rad)
  Width = 1
FEATURE [Part::Box] Box229  label="Cube196"
  AttacherType = Attacher::AttachEngine3D
  Height = 7
  Length = 4
  Placement = pos=(-6,24.4,-2) rot=(0,0,1;0rad)
  Width = 1
FEATURE [Part::Sphere] Sphere072
  Angle1 = -90
  Angle2 = 90
  Angle3 = 360
  AttacherType = Attacher::AttachEngine3D
  Placement = pos=(-7.5,6.5,0.5) rot=(0,0,1;0rad)
  Radius = 1.25
FEATURE [Part::Box] Box230  label="Cube197"
  AttacherType = Attacher::AttachEngine3D
  Height = 7
  Length = 4
  Placement = pos=(-6,36.6,-2) rot=(0,0,1;0rad)
  Width = 1
FEATURE [Part::Box] Box231  label="Cube198"
  AttacherType = Attacher::AttachEngine3D
  Height = 7
  Length = 10
  Placement = pos=(-15,10,-2) rot=(0,0,1;0rad)
  Width = 2
FEATURE [Part::Sphere] Sphere073
  Angle1 = -90
  Angle2 = 90
  Angle3 = 360
  AttacherType = Attacher::AttachEngine3D
  Placement = pos=(-7.5,34,0.5) rot=(0,0,1;0rad)
  Radius = 1.5
FEATURE [Part::Box] Box232  label="Cube199"
  AttacherType = Attacher::AttachEngine3D
  Height = 7
  Length = 4
  Placement = pos=(-6,5,-2) rot=(0,0,1;0rad)
  Width = 1
FEATURE [Part::MultiFuse] Fusion085  label="Extra Holes for Clips006"
  Shapes = -> [Box227,Box228,Box230,Box224,Box229,Box232]
FEATURE [Part::Box] Box233  label="Re-level Edge Clip Block012"
  AttacherType = Attacher::AttachEngine3D
  Height = 10
  Length = 20
  Placement = pos=(-19,-2,3) rot=(0,0,1;0rad)
  Width = 44
FEATURE [Part::Box] Box234  label="Cube200"
  AttacherType = Attacher::AttachEngine3D
  Height = 7
  Length = 10
  Placement = pos=(-15,34.6,-2) rot=(0,0,1;0rad)
  Width = 2
FEATURE [Part::Box] Box235  label="Cube201"
  AttacherType = Attacher::AttachEngine3D
  Height = 7
  Length = 10
  Placement = pos=(-15,25.4,-2) rot=(0,0,1;0rad)
  Width = 2
FEATURE [Part::MultiFuse] Fusion086
  Shapes = -> [Box223,Box226,Box231,Box235,Box234]
FEATURE [Part::Fuse] Fusion087  label="Bumps006"
  Base = -> Sphere072
  Tool = -> Sphere071
FEATURE [Part::Fuse] Fusion084
  Base = -> Fusion087
  Tool = -> Fusion086
FEATURE [Part::Sphere] Sphere074
  Angle1 = -90
  Angle2 = 90
  Angle3 = 360
  AttacherType = Attacher::AttachEngine3D
  Placement = pos=(-7.5,28,0.5) rot=(0,0,1;0rad)
  Radius = 1.5
FEATURE [Part::Fuse] Fusion088  label="Holes006"
  Base = -> Sphere074
  Tool = -> Sphere073
FEATURE [Part::Box] Box236  label="Re-level Edge Clip Block013"
  AttacherType = Attacher::AttachEngine3D
  Height = 10
  Length = 12
  Placement = pos=(-21.5,-2,-7) rot=(0,0,1;0rad)
  Width = 44
FEATURE [Part::Cut] Cut087
  Base = -> Fusion084
  Tool = -> Fusion088
FEATURE [Part::Cut] Cut088
  Base = -> Cut087
  Tool = -> Fusion085
FEATURE [Part::Cut] Cut089
  Base = -> Cut088
  Tool = -> Box233
FEATURE [Part::Cut] Cut090
  Base = -> Cut089
  Tool = -> Box236
FEATURE [Part::Cut] Cut091  label="Edge Clips004"
  Base = -> Cut090
  Placement = pos=(20,-20,0) rot=(0,0,1;1.5708rad)
  Tool = -> Box225
FEATURE [Part::Box] Box237  label="Re-level Edge Clip Block014"
  AttacherType = Attacher::AttachEngine3D
  Height = 10
  Length = 12
  Placement = pos=(-21.5,-2,-7) rot=(0,0,1;0rad)
  Width = 44
FEATURE [Part::Box] Box238  label="Cube202"
  AttacherType = Attacher::AttachEngine3D
  Height = 7
  Length = 4
  Placement = pos=(-6,36.6,-2) rot=(0,0,1;0rad)
  Width = 1
FEATURE [Part::Box] Box239  label="Cube203"
  AttacherType = Attacher::AttachEngine3D
  Height = 7
  Length = 10
  Placement = pos=(-15,10,-2) rot=(0,0,1;0rad)
  Width = 2
FEATURE [Part::Box] Box240  label="Cube204"
  AttacherType = Attacher::AttachEngine3D
  Height = 7
  Length = 10
  Placement = pos=(-15,25.4,-2) rot=(0,0,1;0rad)
  Width = 2
FEATURE [Part::Box] Box241  label="Re-level Edge Clip Block015"
  AttacherType = Attacher::AttachEngine3D
  Height = 10
  Length = 20
  Placement = pos=(-19,-2,3) rot=(0,0,1;0rad)
  Width = 44
FEATURE [Part::Box] Box242  label="Cube205"
  AttacherType = Attacher::AttachEngine3D
  Height = 7
  Length = 10
  Placement = pos=(-15,34.6,-2) rot=(0,0,1;0rad)
  Width = 2
FEATURE [Part::Sphere] Sphere075
  Angle1 = -90
  Angle2 = 90
  Angle3 = 360
  AttacherType = Attacher::AttachEngine3D
  Placement = pos=(-7.5,34,0.5) rot=(0,0,1;0rad)
  Radius = 1.5
FEATURE [Part::Sphere] Sphere076
  Angle1 = -90
  Angle2 = 90
  Angle3 = 360
  AttacherType = Attacher::AttachEngine3D
  Placement = pos=(-7.5,28,0.5) rot=(0,0,1;0rad)
  Radius = 1.5
FEATURE [Part::Fuse] Fusion089  label="Holes007"
  Base = -> Sphere076
  Tool = -> Sphere075
FEATURE [Part::Box] Box243  label="Cube206"
  AttacherType = Attacher::AttachEngine3D
  Height = 7
  Length = 4
  Placement = pos=(-6,5,-2) rot=(0,0,1;0rad)
  Width = 1
FEATURE [Part::Box] Box244  label="Cube207"
  AttacherType = Attacher::AttachEngine3D
  Height = 7
  Length = 4
  Placement = pos=(-6,24.4,-2) rot=(0,0,1;0rad)
  Width = 1
FEATURE [Part::Sphere] Sphere077
  Angle1 = -90
  Angle2 = 90
  Angle3 = 360
  AttacherType = Attacher::AttachEngine3D
  Placement = pos=(-7.5,11.5,0.5) rot=(0,0,1;0rad)
  Radius = 1.25
FEATURE [Part::Box] Box245  label="Cube208"
  AttacherType = Attacher::AttachEngine3D
  Height = 7
  Length = 4
  Placement = pos=(-6,12,-2) rot=(0,0,1;0rad)
  Width = 1
FEATURE [Part::Box] Box246  label="Chamfer Cube007"
  AttacherType = Attacher::AttachEngine3D
  Height = 10
  Length = 13
  Placement = pos=(-11.69,0,-1.19) rot=(0,-1,0;0.785398rad)
  Width = 40
FEATURE [Part::Sphere] Sphere078
  Angle1 = -90
  Angle2 = 90
  Angle3 = 360
  AttacherType = Attacher::AttachEngine3D
  Placement = pos=(-7.5,6.5,0.5) rot=(0,0,1;0rad)
  Radius = 1.25
FEATURE [Part::Fuse] Fusion090  label="Bumps007"
  Base = -> Sphere078
  Tool = -> Sphere077
FEATURE [Part::Box] Box247  label="Cube209"
  AttacherType = Attacher::AttachEngine3D
  Height = 7
  Length = 5
  Placement = pos=(-5,0,-2) rot=(0,0,1;0rad)
  Width = 40
FEATURE [Part::Box] Box248  label="Cube210"
  AttacherType = Attacher::AttachEngine3D
  Height = 7
  Length = 4
  Placement = pos=(-6,27.4,-2) rot=(0,0,1;0rad)
  Width = 7.2
FEATURE [Part::Box] Box249  label="Cube211"
  AttacherType = Attacher::AttachEngine3D
  Height = 7
  Length = 4
  Placement = pos=(-6,8,-2) rot=(0,0,1;0rad)
  Width = 2
FEATURE [Part::MultiFuse] Fusion091  label="Extra Holes for Clips007"
  Shapes = -> [Box248,Box245,Box238,Box249,Box244,Box243]
FEATURE [Part::Box] Box250  label="Cube212"
  AttacherType = Attacher::AttachEngine3D
  Height = 7
  Length = 10
  Placement = pos=(-15,6,-2) rot=(0,0,1;0rad)
  Width = 2
FEATURE [Part::MultiFuse] Fusion092
  Shapes = -> [Box247,Box250,Box239,Box240,Box242]
FEATURE [Part::Fuse] Fusion093
  Base = -> Fusion090
  Tool = -> Fusion092
FEATURE [Part::Cut] Cut093
  Base = -> Fusion093
  Tool = -> Fusion089
FEATURE [Part::Cut] Cut094
  Base = -> Cut093
  Tool = -> Fusion091
FEATURE [Part::Cut] Cut095
  Base = -> Cut094
  Tool = -> Box241
FEATURE [Part::Cut] Cut096
  Base = -> Cut095
  Tool = -> Box237
FEATURE [Part::Cut] Cut092  label="Edge Clips005"
  Base = -> Cut096
  Placement = pos=(20,20,0) rot=(0,0,1;3.14159rad)
  Tool = -> Box246
FEATURE [Part::Box] Box251  label="Re-level Edge Clip Block016"
  AttacherType = Attacher::AttachEngine3D
  Height = 10
  Length = 12
  Placement = pos=(-21.5,-2,-7) rot=(0,0,1;0rad)
  Width = 44
FEATURE [Part::Box] Box252  label="Cube213"
  AttacherType = Attacher::AttachEngine3D
  Height = 7
  Length = 10
  Placement = pos=(-15,10,-2) rot=(0,0,1;0rad)
  Width = 2
FEATURE [Part::Box] Box253  label="Cube214"
  AttacherType = Attacher::AttachEngine3D
  Height = 7
  Length = 4
  Placement = pos=(-6,12,-2) rot=(0,0,1;0rad)
  Width = 1
FEATURE [Part::Box] Box254  label="Chamfer Cube008"
  AttacherType = Attacher::AttachEngine3D
  Height = 10
  Length = 13
  Placement = pos=(-11.69,0,-1.19) rot=(0,-1,0;0.785398rad)
  Width = 40
FEATURE [Part::Sphere] Sphere079
  Angle1 = -90
  Angle2 = 90
  Angle3 = 360
  AttacherType = Attacher::AttachEngine3D
  Placement = pos=(-7.5,6.5,0.5) rot=(0,0,1;0rad)
  Radius = 1.25
FEATURE [Part::Box] Box255  label="Cube215"
  AttacherType = Attacher::AttachEngine3D
  Height = 7
  Length = 5
  Placement = pos=(-5,0,-2) rot=(0,0,1;0rad)
  Width = 40
FEATURE [Part::Box] Box256  label="Cube216"
  AttacherType = Attacher::AttachEngine3D
  Height = 7
  Length = 4
  Placement = pos=(-6,27.4,-2) rot=(0,0,1;0rad)
  Width = 7.2
FEATURE [Part::Box] Box257  label="Cube217"
  AttacherType = Attacher::AttachEngine3D
  Height = 7
  Length = 4
  Placement = pos=(-6,8,-2) rot=(0,0,1;0rad)
  Width = 2
FEATURE [Part::Box] Box258  label="Cube218"
  AttacherType = Attacher::AttachEngine3D
  Height = 7
  Length = 10
  Placement = pos=(-15,6,-2) rot=(0,0,1;0rad)
  Width = 2
FEATURE [Part::Sphere] Sphere080
  Angle1 = -90
  Angle2 = 90
  Angle3 = 360
  AttacherType = Attacher::AttachEngine3D
  Placement = pos=(-7.5,28,0.5) rot=(0,0,1;0rad)
  Radius = 1.5
FEATURE [Part::Box] Box259  label="Cube219"
  AttacherType = Attacher::AttachEngine3D
  Height = 7
  Length = 4
  Placement = pos=(-6,5,-2) rot=(0,0,1;0rad)
  Width = 1
FEATURE [Part::Box] Box260  label="Cube220"
  AttacherType = Attacher::AttachEngine3D
  Height = 7
  Length = 4
  Placement = pos=(-6,24.4,-2) rot=(0,0,1;0rad)
  Width = 1
FEATURE [Part::Sphere] Sphere081
  Angle1 = -90
  Angle2 = 90
  Angle3 = 360
  AttacherType = Attacher::AttachEngine3D
  Placement = pos=(-7.5,11.5,0.5) rot=(0,0,1;0rad)
  Radius = 1.25
FEATURE [Part::Box] Box261  label="Re-level Edge Clip Block017"
  AttacherType = Attacher::AttachEngine3D
  Height = 10
  Length = 20
  Placement = pos=(-19,-2,3) rot=(0,0,1;0rad)
  Width = 44
FEATURE [Part::Box] Box262  label="Cube221"
  AttacherType = Attacher::AttachEngine3D
  Height = 7
  Length = 10
  Placement = pos=(-15,34.6,-2) rot=(0,0,1;0rad)
  Width = 2
FEATURE [Part::Box] Box263  label="Cube222"
  AttacherType = Attacher::AttachEngine3D
  Height = 7
  Length = 10
  Placement = pos=(-15,25.4,-2) rot=(0,0,1;0rad)
  Width = 2
FEATURE [Part::MultiFuse] Fusion096
  Shapes = -> [Box255,Box258,Box252,Box263,Box262]
FEATURE [Part::Box] Box264  label="Cube223"
  AttacherType = Attacher::AttachEngine3D
  Height = 7
  Length = 4
  Placement = pos=(-6,36.6,-2) rot=(0,0,1;0rad)
  Width = 1
FEATURE [Part::MultiFuse] Fusion095  label="Extra Holes for Clips008"
  Shapes = -> [Box256,Box253,Box264,Box257,Box260,Box259]
FEATURE [Part::Fuse] Fusion098  label="Bumps008"
  Base = -> Sphere079
  Tool = -> Sphere081
FEATURE [Part::Fuse] Fusion094
  Base = -> Fusion098
  Tool = -> Fusion096
FEATURE [Part::Sphere] Sphere082
  Angle1 = -90
  Angle2 = 90
  Angle3 = 360
  AttacherType = Attacher::AttachEngine3D
  Placement = pos=(-7.5,34,0.5) rot=(0,0,1;0rad)
  Radius = 1.5
FEATURE [Part::Fuse] Fusion097  label="Holes008"
  Base = -> Sphere080
  Tool = -> Sphere082
FEATURE [Part::Cut] Cut101
  Base = -> Fusion094
  Tool = -> Fusion097
FEATURE [Part::Cut] Cut097
  Base = -> Cut101
  Tool = -> Fusion095
FEATURE [Part::Cut] Cut098
  Base = -> Cut097
  Tool = -> Box261
FEATURE [Part::Cut] Cut099
  Base = -> Cut098
  Tool = -> Box251
FEATURE [Part::Cut] Cut100  label="Edge Clips006"
  Base = -> Cut099
  Placement = pos=(-20,20,0) rot=(0,0,-1;1.5708rad)
  Tool = -> Box254
FEATURE [Part::Box] Box265  label="Cube224"
  AttacherType = Attacher::AttachEngine3D
  Height = 10
  Length = 10
  Placement = pos=(4,-26,1) rot=(0.205904,-0.974848,-0.085288;0.803573rad)
  Width = 15
FEATURE [Part::Box] Box266  label="Cube225"
  AttacherType = Attacher::AttachEngine3D
  Height = 10
  Length = 10
  Placement = pos=(-26,-4,1) rot=(-0.273007,-0.419215,-0.865867;1.78566rad)
  Width = 15
FEATURE [Part::Box] Box267  label="Cube226"
  AttacherType = Attacher::AttachEngine3D
  Height = 10
  Length = 10
  Placement = pos=(-4,26,1) rot=(0.381439,0.080566,0.920876;3.07487rad)
  Width = 15
FEATURE [Part::Box] Box268  label="Cube227"
  AttacherType = Attacher::AttachEngine3D
  Height = 10
  Length = 10
  Placement = pos=(26,4,1) rot=(0.442189,-0.287968,0.849437;1.66134rad)
  Width = 15
FEATURE [Part::MultiFuse] Fusion099  label="Glue Dents001"
  Shapes = -> [Box265,Box266,Box267,Box268]
FEATURE [Part::MultiFuse] Fusion100  label="Edge Clips Fusion001"
  Shapes = -> [Cut100,Cut086,Cut091,Cut092]
FEATURE [Drawing::FeatureViewAnnotation] Annotation001
  Font = Sans
  Rotation = 0
  Scale = 7
  Text = 0.5 rejigged whole thing, stopped clips overhang and moved bump and holes back 0.5
  ViewResult = <g transform="translate(14,30) rotate(0)">\n<text id="Annotation001"\n font-family="Sans"\n font-size="7"\n fill="#000000">\n<tspan x="0" dy="1em">0.5 rejigged whole thing, stopped clips overhang and moved bump and holes back 0.5</tspan>\n</text>\n</g>
  Visible = false
  X = 14
  Y = 30
FEATURE [Part::Cylinder] Cylinder027  label="z-axis"
  Angle = 360
  AttacherType = Attacher::AttachEngine3D
  Height = 73
  Placement = pos=(0,0,-18) rot=(0,0,1;0rad)
  Radius = 0.5
FEATURE [Part::MultiFuse] Fusion101
  Placement = pos=(-15,-15,0) rot=(0,0,1;0rad)
  Shapes = -> [Box069,Cylinder018,Sphere030]
FEATURE [App::DocumentObjectGroup] Group002  label="Old 0.1"
  Group = -> [Sphere027,Sphere028,Sphere029,Sphere031,Sphere032,Sphere033,Sphere034,Cylinder012,Cylinder016,Cylinder015,Cylinder014,Cylinder013,Cylinder017,Cylinder019,Box067,Box073,Box071,Box068,Box070,Box072,Box074]
FEATURE [Part::Box] Box269  label="Square Nut Hole 024"
  AttacherType = Attacher::AttachEngine3D
  Height = 2
  Length = 5.8
  Placement = pos=(-2.9,2.9,2.1) rot=(1,0,0;3.14159rad)
  Width = 5.8
FEATURE [Part::Cylinder] Cylinder028
  Angle = 360
  AttacherType = Attacher::AttachEngine3D
  Height = 10
  Placement = pos=(0,0,6.7) rot=(1,0,0;3.14159rad)
  Radius = 1.7
FEATURE [Part::Sphere] Sphere083
  Angle1 = -90
  Angle2 = 90
  Angle3 = 360
  AttacherType = Attacher::AttachEngine3D
  Placement = pos=(0,0,4.3) rot=(1,0,0;3.14159rad)
  Radius = 3.35
FEATURE [Part::MultiFuse] Fusion102
  Placement = pos=(-15,0,0) rot=(0,0,1;0rad)
  Shapes = -> [Box269,Cylinder028,Sphere083]
FEATURE [Part::Fuse] Fusion103
  Base = -> Fusion101
  Tool = -> Fusion102
FEATURE [Part::Feature] Fusion103001
  Placement = pos=(0,0,0) rot=(0,0,1;1.5708rad)
  shape: bbox 21.7 x 6.7 x 10.95 mm, 18 faces, 2 solids (baked)
FEATURE [Part::Feature] Fusion103002
  Placement = pos=(0,0,0) rot=(0,0,1;3.14159rad)
  shape: bbox 6.7 x 21.7 x 10.95 mm, 18 faces, 2 solids (baked)
FEATURE [Part::Feature] Fusion103003
  Placement = pos=(0,0,0) rot=(0,0,-1;1.5708rad)
  shape: bbox 21.7 x 6.7 x 10.95 mm, 18 faces, 2 solids (baked)
FEATURE [Part::MultiFuse] Fusion103004  label="Nut Holes"
  Shapes = -> [Fusion103,Fusion103001,Fusion103002,Fusion103003]
FEATURE [Part::Fuse] Fusion103005  label="Cube with Edge Clips"
  Base = -> Box075
  Tool = -> Fusion100
FEATURE [Part::Cut] Cut102
  Base = -> Fusion103005
  Tool = -> Fusion099
FEATURE [Part::Cut] Cut103
  Base = -> Cut102
  Tool = -> Fusion103004
FEATURE [Part::Cut] Cut104
  Base = -> Cut103
  Tool = -> Chamfer014
FEATURE [Part::Cut] Cut105
  Base = -> Cut104
  Tool = -> Chamfer013
FEATURE [Part::Cut] Cut106  label="Nut Plate 1.1"
  Base = -> Cut105
  Tool = -> Box145
FEATURE [Part::Fuse] Fusion103006
  Base = -> Cut047
  Tool = -> Fusion076
FEATURE [Part::Cut] Cut107
  Base = -> Fusion103006
  Tool = -> Fusion052
FEATURE [Part::Cut] Cut108
  Base = -> Cut107
  Tool = -> Chamfer008
FEATURE [Part::Cut] Cut109
  Base = -> Cut108
  Tool = -> Box085
FEATURE [Part::Cut] Cut110  label="Ball Plate 1.1"
  Base = -> Cut109
  Tool = -> Fusion078
FEATURE [Drawing::FeatureViewAnnotation] Annotation002
  Font = Sans
  Rotation = 0
  Scale = 7
  ViewResult = <g transform="translate(10,10) rotate(0)">\n<text id="Annotation002"\n font-family="Sans"\n font-size="7"\n fill="#000000">\n<tspan x="0" dy="1em"></tspan>\n</text>\n</g>
  Visible = true
  X = 10
  Y = 10
FEATURE [Drawing::FeatureViewAnnotation] Annotation003
  Font = Sans
  Rotation = 0
  Scale = 7
  Text = 0.5 - > 1.0
  ViewResult = <g transform="translate(14,18) rotate(0)">\n<text id="Annotation003"\n font-family="Sans"\n font-size="7"\n fill="#000000">\n<tspan x="0" dy="1em">0.5 - > 1.0</tspan>\n</text>\n</g>
  Visible = true
  X = 14
  Y = 18
FEATURE [Drawing::FeatureViewAnnotation] Annotation004
  Font = Sans
  Rotation = 0
  Scale = 7
  ViewResult = <g transform="translate(10,10) rotate(0)">\n<text id="Annotation004"\n font-family="Sans"\n font-size="7"\n fill="#000000">\n<tspan x="0" dy="1em"></tspan>\n</text>\n</g>
  Visible = true
  X = 10
  Y = 10
FEATURE [Drawing::FeatureViewAnnotation] Annotation005
  Font = Sans
  Rotation = 0
  Scale = 5
  Text = 0.5 is a working version. 1.0 has everything moved to centre point and then the ball and nut holes moved so that blocks can be mounted in half position
  ViewResult = <g transform="translate(10,30) rotate(0)">\n<text id="Annotation005"\n font-family="Sans"\n font-size="5"\n fill="#000000">\n<tspan x="0" dy="1em">0.5 is a working version. 1.0 has everything moved to centre point and then the ball and nut holes moved so that blocks can be mounted in half position</tspan>\n</text>\n</g>
  Visible = true
  X = 10
  Y = 30
FEATURE [Drawing::FeatureViewAnnotation] Annotation006
  Font = Sans
  Rotation = 0
  Scale = 5
  Text = 1.1 Moved the cube creating the hole with the octagon by 1mm to so distance between pcbs is bigger | Also added holes
  ViewResult = <g transform="translate(10,40) rotate(0)">\n<text id="Annotation006"\n font-family="Sans"\n font-size="5"\n fill="#000000">\n<tspan x="0" dy="1em">1.1 Moved the cube creating the hole with the octagon by 1mm to so distance between pcbs is bigger</tspan>\n<tspan x="0" dy="1em">Also added holes</tspan>\n<tspan x="0" dy="1em"></tspan>\n</text>\n</g>
  Visible = true
  X = 10
  Y = 40
FEATURE [Part::Cylinder] Cylinder029
  Angle = 360
  AttacherType = Attacher::AttachEngine3D
  Height = 10
  Placement = pos=(15,-15,-5) rot=(0,0,1;1.5708rad)
  Radius = 1.7
FEATURE [Part::Sphere] Sphere084  label="Mag Hole001"
  Angle1 = -90
  Angle2 = 90
  Angle3 = 360
  AttacherType = Attacher::AttachEngine3D
  Placement = pos=(15,-15,1.7) rot=(0,0,1;1.5708rad)
  Radius = 2.83
FEATURE [Part::Sphere] Sphere085  label="Mag Hole002"
  Angle1 = -90
  Angle2 = 90
  Angle3 = 360
  AttacherType = Attacher::AttachEngine3D
  Placement = pos=(15,15,1.7) rot=(0,0,1;3.14159rad)
  Radius = 2.83
FEATURE [Part::Sphere] Sphere086  label="Mag Hole 004"
  Angle1 = -90
  Angle2 = 90
  Angle3 = 360
  AttacherType = Attacher::AttachEngine3D
  Placement = pos=(3e-15,15,1.7) rot=(0,0,1;1.5708rad)
  Radius = 2.825
FEATURE [Part::Sphere] Sphere087  label="Mag Hole 005"
  Angle1 = -90
  Angle2 = 90
  Angle3 = 360
  AttacherType = Attacher::AttachEngine3D
  Placement = pos=(-15,2e-15,1.7) rot=(0,0,1;3.14159rad)
  Radius = 2.825
FEATURE [Part::Sphere] Sphere088  label="Mag Hole 006"
  Angle1 = -90
  Angle2 = 90
  Angle3 = 360
  AttacherType = Attacher::AttachEngine3D
  Placement = pos=(-3e-15,-15,1.7) rot=(0,0,-1;1.5708rad)
  Radius = 2.825
FEATURE [Part::Cylinder] Cylinder030
  Angle = 360
  AttacherType = Attacher::AttachEngine3D
  Height = 10
  Placement = pos=(15,15,-5) rot=(0,0,1;3.14159rad)
  Radius = 1.7
FEATURE [Part::Cylinder] Cylinder031
  Angle = 360
  AttacherType = Attacher::AttachEngine3D
  Height = 10
  Placement = pos=(3e-15,15,-5) rot=(0,0,1;1.5708rad)
  Radius = 1.7
FEATURE [Part::Cylinder] Cylinder032
  Angle = 360
  AttacherType = Attacher::AttachEngine3D
  Height = 10
  Placement = pos=(-15,6e-15,-5) rot=(0,0,1;3.14159rad)
  Radius = 1.7
FEATURE [Part::Cylinder] Cylinder033
  Angle = 360
  AttacherType = Attacher::AttachEngine3D
  Height = 10
  Placement = pos=(-9e-15,-15,-5) rot=(0,0,-1;1.5708rad)
  Radius = 1.7
FEATURE [Part::MultiFuse] Fusion103007
  Shapes = -> [Cylinder029,Sphere087,Sphere084,Sphere086,Sphere088,Cylinder032,Cylinder033,Sphere085,Cylinder031,Cylinder030]
FEATURE [Part::Cut] Cut111  label="Ball Plate with Extra Holes"
  Base = -> Cut110
  Tool = -> Fusion103007
FEATURE [Part::Cylinder] Cylinder034
  Angle = 360
  AttacherType = Attacher::AttachEngine3D
  Height = 4
  Placement = pos=(-9.75,-9.75,-3) rot=(0,0,1;0rad)
  Radius = 1.5
FEATURE [Part::Cylinder] Cylinder035
  Angle = 360
  AttacherType = Attacher::AttachEngine3D
  Height = 4
  Placement = pos=(9.75,9.75,-3) rot=(0,0,1;0rad)
  Radius = 1.5
FEATURE [Part::Cylinder] Cylinder036
  Angle = 360
  AttacherType = Attacher::AttachEngine3D
  Height = 4
  Placement = pos=(-9.75,9.75,-3) rot=(0,0,1;0rad)
  Radius = 1.5
FEATURE [Part::Cylinder] Cylinder037
  Angle = 360
  AttacherType = Attacher::AttachEngine3D
  Height = 4
  Placement = pos=(9.75,-9.75,-3) rot=(0,0,1;0rad)
  Radius = 1.5
FEATURE [Part::MultiFuse] Fusion103008
  Shapes = -> [Cylinder034,Cylinder037,Cylinder036,Cylinder035]
FEATURE [Part::Cut] Cut112  label="Ball Plate 1.2"
  Base = -> Cut111
  Tool = -> Fusion103008
FEATURE [Part::Cylinder] Cylinder038
  Angle = 360
  AttacherType = Attacher::AttachEngine3D
  Height = 4
  Placement = pos=(-9.75,-9.75,-3) rot=(0,0,1;0rad)
  Radius = 1.5
FEATURE [Part::Cylinder] Cylinder039
  Angle = 360
  AttacherType = Attacher::AttachEngine3D
  Height = 4
  Placement = pos=(9.75,-9.75,-3) rot=(0,0,1;0rad)
  Radius = 1.5
FEATURE [Part::Cylinder] Cylinder040
  Angle = 360
  AttacherType = Attacher::AttachEngine3D
  Height = 4
  Placement = pos=(-9.75,9.75,-3) rot=(0,0,1;0rad)
  Radius = 1.5
FEATURE [Part::Cylinder] Cylinder041
  Angle = 360
  AttacherType = Attacher::AttachEngine3D
  Height = 4
  Placement = pos=(9.75,9.75,-3) rot=(0,0,1;0rad)
  Radius = 1.5
FEATURE [Part::MultiFuse] Fusion103009
  Shapes = -> [Cylinder038,Cylinder041,Cylinder039,Cylinder040]
FEATURE [Part::Cut] Cut113  label="Nut Plate 1.2"
  Base = -> Cut106
  Tool = -> Fusion103009
FEATURE [Drawing::FeatureViewAnnotation] Annotation007
  Font = Sans
  Rotation = 0
  Scale = 7
  ViewResult = <g transform="translate(10,10) rotate(0)">\n<text id="Annotation007"\n font-family="Sans"\n font-size="7"\n fill="#000000">\n<tspan x="0" dy="1em"></tspan>\n</text>\n</g>
  Visible = true
  X = 10
  Y = 10
FEATURE [Drawing::FeatureViewAnnotation] Annotation008
  Font = Sans
  Rotation = 0
  Scale = 7
  ViewResult = <g transform="translate(10,10) rotate(0)">\n<text id="Annotation008"\n font-family="Sans"\n font-size="7"\n fill="#000000">\n<tspan x="0" dy="1em"></tspan>\n</text>\n</g>
  Visible = true
  X = 10
  Y = 10
FEATURE [Drawing::FeaturePage] Page
  EditableTexts = AUTHOR NAME | CREATION DATE | SUPERVISOR NAME | CHECK DATE | SCALE | WEIGHT | NUMBER | SHEET | TITLE | SUBTITLE
  Group = -> [Annotation,Annotation001,Annotation002,Annotation004,Annotation007,Annotation008]
  Template = <path>
FEATURE [Drawing::FeatureViewAnnotation] Annotation009
  Font = Sans
  Rotation = 0
  Scale = 5
  Text = 1.2 Added holes on the corners of the PCB holes to make it easier to fit
  ViewResult = <g transform="translate(10,50) rotate(0)">\n<text id="Annotation009"\n font-family="Sans"\n font-size="5"\n fill="#000000">\n<tspan x="0" dy="1em">1.1 Moved the cube creating the hole with the octagon by 1mm to so distance between pcbs is bigger</tspan>\n<tspan x="0" dy="1em">Also added holes</tspan>\n<tspan x="0" dy="1em"></tspan>\n</text>\n</g>
  Visible = true
  X = 10
  Y = 50
FEATURE [Drawing::FeaturePage] Page001
  EditableTexts = AUTHOR NAME | CREATION DATE | SUPERVISOR NAME | CHECK DATE | SCALE | WEIGHT | NUMBER | SHEET | TITLE | SUBTITLE
  Group = -> [Annotation003,Annotation005,Annotation006,Annotation009]
  Template = <path>
FEATURE [Part::Feature] Fusion103010
  Placement = pos=(0,0,0) rot=(0,0,-1;1.5708rad)
  shape: bbox 21.7 x 6.7 x 10.95 mm, 18 faces, 2 solids (baked)
FEATURE [Part::Feature] Fusion103011
  Placement = pos=(0,0,0) rot=(0,0,1;3.14159rad)
  shape: bbox 6.7 x 21.7 x 10.95 mm, 18 faces, 2 solids (baked)
FEATURE [Part::Feature] Fusion103012
  Placement = pos=(0,0,0) rot=(0,0,1;1.5708rad)
  shape: bbox 21.7 x 6.7 x 10.95 mm, 18 faces, 2 solids (baked)
FEATURE [Part::Box] Box270  label="Square Nut Hole 025"
  AttacherType = Attacher::AttachEngine3D
  Height = 2
  Length = 5.8
  Placement = pos=(-2.9,2.9,2.1) rot=(1,0,0;3.14159rad)
  Width = 5.8
FEATURE [Part::Cylinder] Cylinder042
  Angle = 360
  AttacherType = Attacher::AttachEngine3D
  Height = 10
  Placement = pos=(0,0,6.7) rot=(1,0,0;3.14159rad)
  Radius = 1.7
FEATURE [Part::Box] Box271  label="Cube228"
  AttacherType = Attacher::AttachEngine3D
  Height = 5
  Length = 40
  Placement = pos=(-20,-20,-2) rot=(0,0,1;0rad)
  Width = 40
FEATURE [Part::Sphere] Sphere089
  Angle1 = -90
  Angle2 = 90
  Angle3 = 360
  AttacherType = Attacher::AttachEngine3D
  Placement = pos=(0,0,4.3) rot=(1,0,0;3.14159rad)
  Radius = 3.35
FEATURE [Part::Box] Box272  label="Cube229"
  AttacherType = Attacher::AttachEngine3D
  Height = 15
  Length = 19.5
  Placement = pos=(-9.75,-9.75,-14) rot=(0,0,1;0rad)
  Width = 19.5
FEATURE [Part::Box] Box273  label="Cube230"
  AttacherType = Attacher::AttachEngine3D
  Height = 15
  Length = 19.5
  Placement = pos=(-9.75,-9.75,-3) rot=(0,0,1;0rad)
  Width = 19.5
FEATURE [Part::Chamfer] Chamfer015  label="Octagon001"
  Base = -> Box273
  Edges = 4 edges r=4: [Edge1,Edge3,Edge5,Edge7]
FEATURE [Part::Box] Box274  label="Cube231"
  AttacherType = Attacher::AttachEngine3D
  Height = 10
  Length = 24
  Placement = pos=(-12,-12,2.1) rot=(0,0,1;0rad)
  Width = 24
FEATURE [Part::Box] Box275  label="Cube232"
  AttacherType = Attacher::AttachEngine3D
  Height = 14
  Length = 20
  Placement = pos=(-10,-10,0) rot=(0,0,1;0rad)
  Width = 20
FEATURE [Part::Cut] Cut116
  Base = -> Box274
  Tool = -> Box275
FEATURE [Part::Chamfer] Chamfer016  label="Glue Channel001"
  Base = -> Cut116
  Edges = 8 edges r=0.95: [Edge4,Edge5,Edge14,Edge16,Edge17,Edge18,Edge19,Edge20]
FEATURE [Part::Box] Box276  label="Cube233"
  AttacherType = Attacher::AttachEngine3D
  Height = 7
  Length = 5
  Placement = pos=(-5,0,-2) rot=(0,0,1;0rad)
  Width = 40
FEATURE [Part::Box] Box277  label="Cube234"
  AttacherType = Attacher::AttachEngine3D
  Height = 7
  Length = 10
  Placement = pos=(-15,6,-2) rot=(0,0,1;0rad)
  Width = 2
FEATURE [Part::Box] Box278  label="Cube235"
  AttacherType = Attacher::AttachEngine3D
  Height = 7
  Length = 10
  Placement = pos=(-15,10,-2) rot=(0,0,1;0rad)
  Width = 2
FEATURE [Part::Box] Box279  label="Cube236"
  AttacherType = Attacher::AttachEngine3D
  Height = 7
  Length = 10
  Placement = pos=(-15,25.4,-2) rot=(0,0,1;0rad)
  Width = 2
FEATURE [Part::Box] Box280  label="Cube237"
  AttacherType = Attacher::AttachEngine3D
  Height = 7
  Length = 10
  Placement = pos=(-15,34.6,-2) rot=(0,0,1;0rad)
  Width = 2
FEATURE [Part::Sphere] Sphere090
  Angle1 = -90
  Angle2 = 90
  Angle3 = 360
  AttacherType = Attacher::AttachEngine3D
  Placement = pos=(-7.5,6.5,0.5) rot=(0,0,1;0rad)
  Radius = 1.25
FEATURE [Part::Box] Box281  label="Chamfer Cube009"
  AttacherType = Attacher::AttachEngine3D
  Height = 10
  Length = 13
  Placement = pos=(-11.69,0,-1.19) rot=(0,-1,0;0.785398rad)
  Width = 40
FEATURE [Part::Sphere] Sphere091
  Angle1 = -90
  Angle2 = 90
  Angle3 = 360
  AttacherType = Attacher::AttachEngine3D
  Placement = pos=(-7.5,11.5,0.5) rot=(0,0,1;0rad)
  Radius = 1.25
FEATURE [Part::Sphere] Sphere092
  Angle1 = -90
  Angle2 = 90
  Angle3 = 360
  AttacherType = Attacher::AttachEngine3D
  Placement = pos=(-7.5,28,0.5) rot=(0,0,1;0rad)
  Radius = 1.5
FEATURE [Part::Sphere] Sphere093
  Angle1 = -90
  Angle2 = 90
  Angle3 = 360
  AttacherType = Attacher::AttachEngine3D
  Placement = pos=(-7.5,34,0.5) rot=(0,0,1;0rad)
  Radius = 1.5
FEATURE [Part::Box] Box282  label="Cube238"
  AttacherType = Attacher::AttachEngine3D
  Height = 7
  Length = 4
  Placement = pos=(-6,5,-2) rot=(0,0,1;0rad)
  Width = 1
FEATURE [Part::Box] Box283  label="Cube239"
  AttacherType = Attacher::AttachEngine3D
  Height = 7
  Length = 4
  Placement = pos=(-6,8,-2) rot=(0,0,1;0rad)
  Width = 2
FEATURE [Part::Box] Box284  label="Cube240"
  AttacherType = Attacher::AttachEngine3D
  Height = 7
  Length = 4
  Placement = pos=(-6,12,-2) rot=(0,0,1;0rad)
  Width = 1
FEATURE [Part::Box] Box285  label="Cube241"
  AttacherType = Attacher::AttachEngine3D
  Height = 7
  Length = 4
  Placement = pos=(-6,24.4,-2) rot=(0,0,1;0rad)
  Width = 1
FEATURE [Part::Box] Box286  label="Cube242"
  AttacherType = Attacher::AttachEngine3D
  Height = 7
  Length = 4
  Placement = pos=(-6,36.6,-2) rot=(0,0,1;0rad)
  Width = 1
FEATURE [Part::Box] Box287  label="Cube243"
  AttacherType = Attacher::AttachEngine3D
  Height = 7
  Length = 4
  Placement = pos=(-6,27.4,-2) rot=(0,0,1;0rad)
  Width = 7.2
FEATURE [Part::MultiFuse] Fusion103013  label="Extra Holes for Clips009"
  Shapes = -> [Box287,Box284,Box286,Box283,Box285,Box282]
FEATURE [Part::Box] Box288  label="Re-level Edge Clip Block018"
  AttacherType = Attacher::AttachEngine3D
  Height = 10
  Length = 20
  Placement = pos=(-19,-2,3) rot=(0,0,1;0rad)
  Width = 44
FEATURE [Part::Box] Box289  label="Re-level Edge Clip Block019"
  AttacherType = Attacher::AttachEngine3D
  Height = 10
  Length = 12
  Placement = pos=(-21.5,-2,-7) rot=(0,0,1;0rad)
  Width = 44
FEATURE [Part::Fuse] Fusion103014  label="Bumps009"
  Base = -> Sphere090
  Tool = -> Sphere091
FEATURE [Part::Fuse] Fusion103015  label="Holes009"
  Base = -> Sphere092
  Tool = -> Sphere093
FEATURE [Part::MultiFuse] Fusion103016
  Shapes = -> [Box276,Box277,Box278,Box279,Box280]
FEATURE [Part::Fuse] Fusion103017
  Base = -> Fusion103014
  Tool = -> Fusion103016
FEATURE [Part::Cut] Cut117
  Base = -> Fusion103017
  Tool = -> Fusion103015
FEATURE [Part::Cut] Cut118
  Base = -> Cut117
  Tool = -> Fusion103013
FEATURE [Part::Cut] Cut119
  Base = -> Cut118
  Tool = -> Box288
FEATURE [Part::Cut] Cut120
  Base = -> Cut119
  Tool = -> Box289
FEATURE [Part::Cut] Cut121  label="Edge Clips Master002"
  Base = -> Cut120
  Placement = pos=(-20,-20,0) rot=(0,0,1;0rad)
  Tool = -> Box281
FEATURE [Part::Box] Box290  label="Cube244"
  AttacherType = Attacher::AttachEngine3D
  Height = 7
  Length = 5
  Placement = pos=(-5,0,-2) rot=(0,0,1;0rad)
  Width = 40
FEATURE [Part::Box] Box291  label="Cube245"
  AttacherType = Attacher::AttachEngine3D
  Height = 7
  Length = 4
  Placement = pos=(-6,8,-2) rot=(0,0,1;0rad)
  Width = 2
FEATURE [Part::Box] Box292  label="Chamfer Cube010"
  AttacherType = Attacher::AttachEngine3D
  Height = 10
  Length = 13
  Placement = pos=(-11.69,0,-1.19) rot=(0,-1,0;0.785398rad)
  Width = 40
FEATURE [Part::Box] Box293  label="Cube246"
  AttacherType = Attacher::AttachEngine3D
  Height = 7
  Length = 10
  Placement = pos=(-15,6,-2) rot=(0,0,1;0rad)
  Width = 2
FEATURE [Part::Sphere] Sphere094
  Angle1 = -90
  Angle2 = 90
  Angle3 = 360
  AttacherType = Attacher::AttachEngine3D
  Placement = pos=(-7.5,11.5,0.5) rot=(0,0,1;0rad)
  Radius = 1.25
FEATURE [Part::Box] Box294  label="Cube247"
  AttacherType = Attacher::AttachEngine3D
  Height = 7
  Length = 4
  Placement = pos=(-6,27.4,-2) rot=(0,0,1;0rad)
  Width = 7.2
FEATURE [Part::Box] Box295  label="Cube248"
  AttacherType = Attacher::AttachEngine3D
  Height = 7
  Length = 4
  Placement = pos=(-6,12,-2) rot=(0,0,1;0rad)
  Width = 1
FEATURE [Part::Box] Box296  label="Cube249"
  AttacherType = Attacher::AttachEngine3D
  Height = 7
  Length = 4
  Placement = pos=(-6,24.4,-2) rot=(0,0,1;0rad)
  Width = 1
FEATURE [Part::Sphere] Sphere095
  Angle1 = -90
  Angle2 = 90
  Angle3 = 360
  AttacherType = Attacher::AttachEngine3D
  Placement = pos=(-7.5,6.5,0.5) rot=(0,0,1;0rad)
  Radius = 1.25
FEATURE [Part::Box] Box297  label="Cube250"
  AttacherType = Attacher::AttachEngine3D
  Height = 7
  Length = 4
  Placement = pos=(-6,36.6,-2) rot=(0,0,1;0rad)
  Width = 1
FEATURE [Part::Box] Box298  label="Cube251"
  AttacherType = Attacher::AttachEngine3D
  Height = 7
  Length = 10
  Placement = pos=(-15,10,-2) rot=(0,0,1;0rad)
  Width = 2
FEATURE [Part::Sphere] Sphere096
  Angle1 = -90
  Angle2 = 90
  Angle3 = 360
  AttacherType = Attacher::AttachEngine3D
  Placement = pos=(-7.5,34,0.5) rot=(0,0,1;0rad)
  Radius = 1.5
FEATURE [Part::Box] Box299  label="Cube252"
  AttacherType = Attacher::AttachEngine3D
  Height = 7
  Length = 4
  Placement = pos=(-6,5,-2) rot=(0,0,1;0rad)
  Width = 1
FEATURE [Part::MultiFuse] Fusion103019  label="Extra Holes for Clips010"
  Shapes = -> [Box294,Box295,Box297,Box291,Box296,Box299]
FEATURE [Part::Box] Box300  label="Re-level Edge Clip Block020"
  AttacherType = Attacher::AttachEngine3D
  Height = 10
  Length = 20
  Placement = pos=(-19,-2,3) rot=(0,0,1;0rad)
  Width = 44
FEATURE [Part::Box] Box301  label="Cube253"
  AttacherType = Attacher::AttachEngine3D
  Height = 7
  Length = 10
  Placement = pos=(-15,34.6,-2) rot=(0,0,1;0rad)
  Width = 2
FEATURE [Part::Box] Box302  label="Cube254"
  AttacherType = Attacher::AttachEngine3D
  Height = 7
  Length = 10
  Placement = pos=(-15,25.4,-2) rot=(0,0,1;0rad)
  Width = 2
FEATURE [Part::MultiFuse] Fusion103020
  Shapes = -> [Box290,Box293,Box298,Box302,Box301]
FEATURE [Part::Fuse] Fusion103021  label="Bumps010"
  Base = -> Sphere095
  Tool = -> Sphere094
FEATURE [Part::Fuse] Fusion103018
  Base = -> Fusion103021
  Tool = -> Fusion103020
FEATURE [Part::Sphere] Sphere097
  Angle1 = -90
  Angle2 = 90
  Angle3 = 360
  AttacherType = Attacher::AttachEngine3D
  Placement = pos=(-7.5,28,0.5) rot=(0,0,1;0rad)
  Radius = 1.5
FEATURE [Part::Fuse] Fusion103022  label="Holes010"
  Base = -> Sphere097
  Tool = -> Sphere096
FEATURE [Part::Box] Box303  label="Re-level Edge Clip Block021"
  AttacherType = Attacher::AttachEngine3D
  Height = 10
  Length = 12
  Placement = pos=(-21.5,-2,-7) rot=(0,0,1;0rad)
  Width = 44
FEATURE [Part::Cut] Cut122
  Base = -> Fusion103018
  Tool = -> Fusion103022
FEATURE [Part::Cut] Cut123
  Base = -> Cut122
  Tool = -> Fusion103019
FEATURE [Part::Cut] Cut124
  Base = -> Cut123
  Tool = -> Box300
FEATURE [Part::Cut] Cut125
  Base = -> Cut124
  Tool = -> Box303
FEATURE [Part::Cut] Cut126  label="Edge Clips007"
  Base = -> Cut125
  Placement = pos=(20,-20,0) rot=(0,0,1;1.5708rad)
  Tool = -> Box292
FEATURE [Part::Box] Box304  label="Re-level Edge Clip Block022"
  AttacherType = Attacher::AttachEngine3D
  Height = 10
  Length = 12
  Placement = pos=(-21.5,-2,-7) rot=(0,0,1;0rad)
  Width = 44
FEATURE [Part::Box] Box305  label="Cube255"
  AttacherType = Attacher::AttachEngine3D
  Height = 7
  Length = 4
  Placement = pos=(-6,36.6,-2) rot=(0,0,1;0rad)
  Width = 1
FEATURE [Part::Box] Box306  label="Cube256"
  AttacherType = Attacher::AttachEngine3D
  Height = 7
  Length = 10
  Placement = pos=(-15,10,-2) rot=(0,0,1;0rad)
  Width = 2
FEATURE [Part::Box] Box307  label="Cube257"
  AttacherType = Attacher::AttachEngine3D
  Height = 7
  Length = 10
  Placement = pos=(-15,25.4,-2) rot=(0,0,1;0rad)
  Width = 2
FEATURE [Part::Box] Box308  label="Re-level Edge Clip Block023"
  AttacherType = Attacher::AttachEngine3D
  Height = 10
  Length = 20
  Placement = pos=(-19,-2,3) rot=(0,0,1;0rad)
  Width = 44
FEATURE [Part::Box] Box309  label="Cube258"
  AttacherType = Attacher::AttachEngine3D
  Height = 7
  Length = 10
  Placement = pos=(-15,34.6,-2) rot=(0,0,1;0rad)
  Width = 2
FEATURE [Part::Sphere] Sphere098
  Angle1 = -90
  Angle2 = 90
  Angle3 = 360
  AttacherType = Attacher::AttachEngine3D
  Placement = pos=(-7.5,34,0.5) rot=(0,0,1;0rad)
  Radius = 1.5
FEATURE [Part::Sphere] Sphere099
  Angle1 = -90
  Angle2 = 90
  Angle3 = 360
  AttacherType = Attacher::AttachEngine3D
  Placement = pos=(-7.5,28,0.5) rot=(0,0,1;0rad)
  Radius = 1.5
FEATURE [Part::Fuse] Fusion103023  label="Holes011"
  Base = -> Sphere099
  Tool = -> Sphere098
FEATURE [Part::Box] Box310  label="Cube259"
  AttacherType = Attacher::AttachEngine3D
  Height = 7
  Length = 4
  Placement = pos=(-6,5,-2) rot=(0,0,1;0rad)
  Width = 1
FEATURE [Part::Box] Box311  label="Cube260"
  AttacherType = Attacher::AttachEngine3D
  Height = 7
  Length = 4
  Placement = pos=(-6,24.4,-2) rot=(0,0,1;0rad)
  Width = 1
FEATURE [Part::Sphere] Sphere100
  Angle1 = -90
  Angle2 = 90
  Angle3 = 360
  AttacherType = Attacher::AttachEngine3D
  Placement = pos=(-7.5,11.5,0.5) rot=(0,0,1;0rad)
  Radius = 1.25
FEATURE [Part::Box] Box312  label="Cube261"
  AttacherType = Attacher::AttachEngine3D
  Height = 7
  Length = 4
  Placement = pos=(-6,12,-2) rot=(0,0,1;0rad)
  Width = 1
FEATURE [Part::Box] Box313  label="Chamfer Cube011"
  AttacherType = Attacher::AttachEngine3D
  Height = 10
  Length = 13
  Placement = pos=(-11.69,0,-1.19) rot=(0,-1,0;0.785398rad)
  Width = 40
FEATURE [Part::Sphere] Sphere101
  Angle1 = -90
  Angle2 = 90
  Angle3 = 360
  AttacherType = Attacher::AttachEngine3D
  Placement = pos=(-7.5,6.5,0.5) rot=(0,0,1;0rad)
  Radius = 1.25
FEATURE [Part::Fuse] Fusion103024  label="Bumps011"
  Base = -> Sphere101
  Tool = -> Sphere100
FEATURE [Part::Box] Box314  label="Cube262"
  AttacherType = Attacher::AttachEngine3D
  Height = 7
  Length = 5
  Placement = pos=(-5,0,-2) rot=(0,0,1;0rad)
  Width = 40
FEATURE [Part::Box] Box315  label="Cube263"
  AttacherType = Attacher::AttachEngine3D
  Height = 7
  Length = 4
  Placement = pos=(-6,27.4,-2) rot=(0,0,1;0rad)
  Width = 7.2
FEATURE [Part::Box] Box316  label="Cube264"
  AttacherType = Attacher::AttachEngine3D
  Height = 7
  Length = 4
  Placement = pos=(-6,8,-2) rot=(0,0,1;0rad)
  Width = 2
FEATURE [Part::MultiFuse] Fusion103025  label="Extra Holes for Clips011"
  Shapes = -> [Box315,Box312,Box305,Box316,Box311,Box310]
FEATURE [Part::Box] Box317  label="Cube265"
  AttacherType = Attacher::AttachEngine3D
  Height = 7
  Length = 10
  Placement = pos=(-15,6,-2) rot=(0,0,1;0rad)
  Width = 2
FEATURE [Part::MultiFuse] Fusion103026
  Shapes = -> [Box314,Box317,Box306,Box307,Box309]
FEATURE [Part::Fuse] Fusion103027
  Base = -> Fusion103024
  Tool = -> Fusion103026
FEATURE [Part::Cut] Cut128
  Base = -> Fusion103027
  Tool = -> Fusion103023
FEATURE [Part::Cut] Cut114
  Base = -> Cut128
  Tool = -> Fusion103025
FEATURE [Part::Cut] Cut129
  Base = -> Cut114
  Tool = -> Box308
FEATURE [Part::Cut] Cut115
  Base = -> Cut129
  Tool = -> Box304
FEATURE [Part::Cut] Cut127  label="Edge Clips008"
  Base = -> Cut115
  Placement = pos=(20,20,0) rot=(0,0,1;3.14159rad)
  Tool = -> Box313
FEATURE [Part::Box] Box318  label="Re-level Edge Clip Block024"
  AttacherType = Attacher::AttachEngine3D
  Height = 10
  Length = 12
  Placement = pos=(-21.5,-2,-7) rot=(0,0,1;0rad)
  Width = 44
FEATURE [Part::Box] Box319  label="Cube266"
  AttacherType = Attacher::AttachEngine3D
  Height = 7
  Length = 10
  Placement = pos=(-15,10,-2) rot=(0,0,1;0rad)
  Width = 2
FEATURE [Part::Box] Box320  label="Cube267"
  AttacherType = Attacher::AttachEngine3D
  Height = 7
  Length = 4
  Placement = pos=(-6,12,-2) rot=(0,0,1;0rad)
  Width = 1
FEATURE [Part::Box] Box321  label="Chamfer Cube012"
  AttacherType = Attacher::AttachEngine3D
  Height = 10
  Length = 13
  Placement = pos=(-11.69,0,-1.19) rot=(0,-1,0;0.785398rad)
  Width = 40
FEATURE [Part::Sphere] Sphere102
  Angle1 = -90
  Angle2 = 90
  Angle3 = 360
  AttacherType = Attacher::AttachEngine3D
  Placement = pos=(-7.5,6.5,0.5) rot=(0,0,1;0rad)
  Radius = 1.25
FEATURE [Part::Box] Box322  label="Cube268"
  AttacherType = Attacher::AttachEngine3D
  Height = 7
  Length = 5
  Placement = pos=(-5,0,-2) rot=(0,0,1;0rad)
  Width = 40
FEATURE [Part::Box] Box323  label="Cube269"
  AttacherType = Attacher::AttachEngine3D
  Height = 7
  Length = 4
  Placement = pos=(-6,27.4,-2) rot=(0,0,1;0rad)
  Width = 7.2
FEATURE [Part::Box] Box324  label="Cube270"
  AttacherType = Attacher::AttachEngine3D
  Height = 7
  Length = 4
  Placement = pos=(-6,8,-2) rot=(0,0,1;0rad)
  Width = 2
FEATURE [Part::Box] Box325  label="Cube271"
  AttacherType = Attacher::AttachEngine3D
  Height = 7
  Length = 10
  Placement = pos=(-15,6,-2) rot=(0,0,1;0rad)
  Width = 2
FEATURE [Part::Sphere] Sphere103
  Angle1 = -90
  Angle2 = 90
  Angle3 = 360
  AttacherType = Attacher::AttachEngine3D
  Placement = pos=(-7.5,28,0.5) rot=(0,0,1;0rad)
  Radius = 1.5
FEATURE [Part::Box] Box326  label="Cube272"
  AttacherType = Attacher::AttachEngine3D
  Height = 7
  Length = 4
  Placement = pos=(-6,5,-2) rot=(0,0,1;0rad)
  Width = 1
FEATURE [Part::Box] Box327  label="Cube273"
  AttacherType = Attacher::AttachEngine3D
  Height = 7
  Length = 4
  Placement = pos=(-6,24.4,-2) rot=(0,0,1;0rad)
  Width = 1
FEATURE [Part::Sphere] Sphere104
  Angle1 = -90
  Angle2 = 90
  Angle3 = 360
  AttacherType = Attacher::AttachEngine3D
  Placement = pos=(-7.5,11.5,0.5) rot=(0,0,1;0rad)
  Radius = 1.25
FEATURE [Part::Box] Box328  label="Re-level Edge Clip Block025"
  AttacherType = Attacher::AttachEngine3D
  Height = 10
  Length = 20
  Placement = pos=(-19,-2,3) rot=(0,0,1;0rad)
  Width = 44
FEATURE [Part::Box] Box329  label="Cube274"
  AttacherType = Attacher::AttachEngine3D
  Height = 7
  Length = 10
  Placement = pos=(-15,34.6,-2) rot=(0,0,1;0rad)
  Width = 2
FEATURE [Part::Box] Box330  label="Cube275"
  AttacherType = Attacher::AttachEngine3D
  Height = 7
  Length = 10
  Placement = pos=(-15,25.4,-2) rot=(0,0,1;0rad)
  Width = 2
FEATURE [Part::MultiFuse] Fusion103030
  Shapes = -> [Box322,Box325,Box319,Box330,Box329]
FEATURE [Part::Box] Box331  label="Cube276"
  AttacherType = Attacher::AttachEngine3D
  Height = 7
  Length = 4
  Placement = pos=(-6,36.6,-2) rot=(0,0,1;0rad)
  Width = 1
FEATURE [Part::MultiFuse] Fusion103029  label="Extra Holes for Clips012"
  Shapes = -> [Box323,Box320,Box331,Box324,Box327,Box326]
FEATURE [Part::Fuse] Fusion103032  label="Bumps012"
  Base = -> Sphere102
  Tool = -> Sphere104
FEATURE [Part::Fuse] Fusion103028
  Base = -> Fusion103032
  Tool = -> Fusion103030
FEATURE [Part::Sphere] Sphere105
  Angle1 = -90
  Angle2 = 90
  Angle3 = 360
  AttacherType = Attacher::AttachEngine3D
  Placement = pos=(-7.5,34,0.5) rot=(0,0,1;0rad)
  Radius = 1.5
FEATURE [Part::Fuse] Fusion103031  label="Holes012"
  Base = -> Sphere103
  Tool = -> Sphere105
FEATURE [Part::Cut] Cut134
  Base = -> Fusion103028
  Tool = -> Fusion103031
FEATURE [Part::Cut] Cut130
  Base = -> Cut134
  Tool = -> Fusion103029
FEATURE [Part::Cut] Cut131
  Base = -> Cut130
  Tool = -> Box328
FEATURE [Part::Cut] Cut132
  Base = -> Cut131
  Tool = -> Box318
FEATURE [Part::Cut] Cut133  label="Edge Clips009"
  Base = -> Cut132
  Placement = pos=(-20,20,0) rot=(0,0,-1;1.5708rad)
  Tool = -> Box321
FEATURE [Part::Box] Box332  label="Cube277"
  AttacherType = Attacher::AttachEngine3D
  Height = 10
  Length = 10
  Placement = pos=(4,-26,1) rot=(0.205904,-0.974848,-0.085288;0.803573rad)
  Width = 15
FEATURE [Part::Box] Box333  label="Cube278"
  AttacherType = Attacher::AttachEngine3D
  Height = 10
  Length = 10
  Placement = pos=(-26,-4,1) rot=(-0.273007,-0.419215,-0.865867;1.78566rad)
  Width = 15
FEATURE [Part::Box] Box334  label="Cube279"
  AttacherType = Attacher::AttachEngine3D
  Height = 10
  Length = 10
  Placement = pos=(-4,26,1) rot=(0.381439,0.080566,0.920876;3.07487rad)
  Width = 15
FEATURE [Part::Box] Box335  label="Cube280"
  AttacherType = Attacher::AttachEngine3D
  Height = 10
  Length = 10
  Placement = pos=(26,4,1) rot=(0.442189,-0.287968,0.849437;1.66134rad)
  Width = 15
FEATURE [Part::MultiFuse] Fusion103033  label="Glue Dents002"
  Shapes = -> [Box332,Box333,Box334,Box335]
FEATURE [Part::MultiFuse] Fusion103034  label="Edge Clips Fusion002"
  Shapes = -> [Cut133,Cut121,Cut126,Cut127]
FEATURE [Part::MultiFuse] Fusion103035
  Placement = pos=(-15,-15,0) rot=(0,0,1;0rad)
  Shapes = -> [Box270,Cylinder042,Sphere089]
FEATURE [Part::Box] Box336  label="Square Nut Hole 026"
  AttacherType = Attacher::AttachEngine3D
  Height = 2
  Length = 5.8
  Placement = pos=(-2.9,2.9,2.1) rot=(1,0,0;3.14159rad)
  Width = 5.8
FEATURE [Part::Cylinder] Cylinder043
  Angle = 360
  AttacherType = Attacher::AttachEngine3D
  Height = 10
  Placement = pos=(0,0,6.7) rot=(1,0,0;3.14159rad)
  Radius = 1.7
FEATURE [Part::Sphere] Sphere106
  Angle1 = -90
  Angle2 = 90
  Angle3 = 360
  AttacherType = Attacher::AttachEngine3D
  Placement = pos=(0,0,4.3) rot=(1,0,0;3.14159rad)
  Radius = 3.35
FEATURE [Part::MultiFuse] Fusion103036
  Placement = pos=(-15,0,0) rot=(0,0,1;0rad)
  Shapes = -> [Box336,Cylinder043,Sphere106]
FEATURE [Part::Fuse] Fusion103037
  Base = -> Fusion103035
  Tool = -> Fusion103036
FEATURE [Part::MultiFuse] Fusion103038  label="Nut Holes001"
  Shapes = -> [Fusion103037,Fusion103012,Fusion103011,Fusion103010]
FEATURE [Part::Fuse] Fusion103039  label="Cube with Edge Clips001"
  Base = -> Box271
  Tool = -> Fusion103034
FEATURE [Part::Cut] Cut135
  Base = -> Fusion103039
  Tool = -> Fusion103033
FEATURE [Part::Cut] Cut136
  Base = -> Cut135
  Tool = -> Fusion103038
FEATURE [Part::Cut] Cut137
  Base = -> Cut136
  Tool = -> Chamfer016
FEATURE [Part::Cut] Cut138
  Base = -> Cut137
  Tool = -> Chamfer015
FEATURE [Part::Cut] Cut139  label="Nut Plate 1.003"
  Base = -> Cut138
  Tool = -> Box272
FEATURE [Part::Cylinder] Cylinder044
  Angle = 360
  AttacherType = Attacher::AttachEngine3D
  Height = 4
  Placement = pos=(-9.75,-9.75,-3) rot=(0,0,1;0rad)
  Radius = 1.5
FEATURE [Part::Cylinder] Cylinder045
  Angle = 360
  AttacherType = Attacher::AttachEngine3D
  Height = 4
  Placement = pos=(9.75,-9.75,-3) rot=(0,0,1;0rad)
  Radius = 1.5
FEATURE [Part::Cylinder] Cylinder046
  Angle = 360
  AttacherType = Attacher::AttachEngine3D
  Height = 4
  Placement = pos=(-9.75,9.75,-3) rot=(0,0,1;0rad)
  Radius = 1.5
FEATURE [Part::Cylinder] Cylinder047
  Angle = 360
  AttacherType = Attacher::AttachEngine3D
  Height = 4
  Placement = pos=(9.75,9.75,-3) rot=(0,0,1;0rad)
  Radius = 1.5
FEATURE [Part::MultiFuse] Fusion103040
  Shapes = -> [Cylinder044,Cylinder047,Cylinder045,Cylinder046]
FEATURE [Part::Cut] Cut140  label="Nut Plate 1.004"
  Base = -> Cut139
  Placement = pos=(0,0,-6) rot=(0,0,1;0rad)
  Tool = -> Fusion103040
FEATURE [App::DocumentObjectGroup] Group003  label="Cube-components"
  Group = -> [Cut112,Cut113]
FEATURE [Part::Box] Box404  label="Cube334"
  AttacherType = Attacher::AttachEngine3D
  Height = 14
  Length = 5
  Placement = pos=(20,20,-7) rot=(0,0,1;0rad)
  Width = 5
FEATURE [Part::Box] Box405  label="Cube335"
  AttacherType = Attacher::AttachEngine3D
  Height = 13
  Length = 15
  Placement = pos=(10,10,2) rot=(0,0,1;0rad)
  Width = 15
FEATURE [Part::FeaturePython] BevelGear001  # WARN: FeaturePython — macro-defined, semantics opaque (R4)
  Placement = pos=(7.81,7.81,10.5) rot=(0.862856,-0.357407,-0.357407;1.71777rad)
  backlash = 0
  beta = 0
  clearance = 0.1
  height = 3
  m = 1
  numpoints = 6
  pitch_angle = 45
  pressure_angle = 20
  reset_origin = true
  teeth = 10
FEATURE [Part::Cylinder] Cylinder054
  Angle = 360
  AttacherType = Attacher::AttachEngine3D
  Height = 22
  Radius = 11
FEATURE [Part::Cone] Cone
  Angle = 360
  AttacherType = Attacher::AttachEngine3D
  Height = 9
  Placement = pos=(8.52,8.52,10.5) rot=(0.862856,-0.357407,-0.357407;1.71777rad)
  Radius1 = 8
  Radius2 = 1.5
FEATURE [Part::Box] Box406004  label="Square Nut Hole 029"
  AttacherType = Attacher::AttachEngine3D
  Height = 2
  Length = 5.8
  Placement = pos=(15.7,19.8,7.6) rot=(0.862856,-0.357407,-0.357407;1.71777rad)
  Width = 14.8
FEATURE [Part::Box] Box406005  label="60mm-high"
  AttacherType = Attacher::AttachEngine3D
  Height = 60
  Length = 10
  Placement = pos=(-29,12,-3) rot=(0,0,1;0rad)
  Width = 10
FEATURE [Part::Cylinder] Cylinder057  label="small-gear-hub"
  Angle = 360
  AttacherType = Attacher::AttachEngine3D
  Height = 5
  Placement = pos=(7.5,7.5,10.5) rot=(0.862856,-0.357407,-0.357407;1.71777rad)
  Radius = 4
FEATURE [Part::Feature] Shape001  label="M3-hex-cavity"
  Placement = pos=(-0.5,-0.5,10.5) rot=(0.281085,0.678598,0.678598;2.59356rad)
  shape: bbox 11.56 x 11.56 x 5.5 mm, 8 faces (baked)
FEATURE [Part::Cylinder] Cylinder058  label="M3-screw-drive001"
  Angle = 360
  AttacherType = Attacher::AttachEngine3D
  Height = 33
  Placement = pos=(23.37,23.37,10.5) rot=(0.862856,-0.357407,-0.357407;1.71777rad)
  Radius = 1.75
FEATURE [Part::Box] Box406007  label="Cube338"
  AttacherType = Attacher::AttachEngine3D
  Height = 14
  Length = 14
  Placement = pos=(1.78,11.68,2) rot=(0,0,-1;0.785398rad)
  Width = 10
FEATURE [Part::Box] Box406008  label="slot-1"
  AttacherType = Attacher::AttachEngine3D
  Height = 36
  Length = 10.5
  Placement = pos=(10.22,17.65,0) rot=(0,0,-1;0.785398rad)
  Width = 28
FEATURE [Part::Cylinder] Cylinder059  label="M3-screw-drive002"
  Angle = 360
  AttacherType = Attacher::AttachEngine3D
  Height = 80
  Placement = pos=(26.8701,26.8701,10.5) rot=(0.862856,-0.357407,-0.357407;1.71777rad)
  Radius = 2.15
FEATURE [Part::Cylinder] Cylinder066  label="M3-screw-drive003"
  Angle = 360
  AttacherType = Attacher::AttachEngine3D
  Height = 33
  Placement = pos=(26.8701,26.8701,10.5) rot=(0.862856,-0.357407,-0.357407;1.71777rad)
  Radius = 1.75
FEATURE [Part::MultiFuse] Fusion103077010  label="finger-cavity"
  Shapes = -> [Cylinder066,Box406004]
FEATURE [Part::Box] Box406015  label="motor-clamp-0"
  AttacherType = Attacher::AttachEngine3D
  Height = 31
  Length = 53.28
  Placement = pos=(-13.8876,-23.7871,2) rot=(0,0,1;0.785398rad)
  Width = 14
FEATURE [Part::Box] Box406016  label="clamp-slot"
  AttacherType = Attacher::AttachEngine3D
  Height = 21
  Length = 49
  Placement = pos=(-15.9,-17.31,17) rot=(0,0,1;0.785398rad)
  Width = 2
FEATURE [Part::Cylinder] Cylinder067
  Angle = 360
  AttacherType = Attacher::AttachEngine3D
  Height = 15
  Placement = pos=(0,0,9) rot=(0,0,1;0rad)
  Radius = 6.25
FEATURE [Part::Box] Box406017  label="gearbox001"
  AttacherType = Attacher::AttachEngine3D
  Height = 27
  Length = 16
  Placement = pos=(-8,-5.25,0) rot=(0,0,1;0rad)
  Width = 10.5
FEATURE [Part::MultiCommon] Common004  label="motor-hole"
  Placement = pos=(0,0,11) rot=(0,0,-1;0.785398rad)
  Shapes = -> [Cylinder067,Box406017]
FEATURE [Part::Cylinder] Cylinder068
  Angle = 360
  AttacherType = Attacher::AttachEngine3D
  Height = 12
  Radius = 1.2
FEATURE [Part::Cylinder] Cylinder069
  Angle = 360
  AttacherType = Attacher::AttachEngine3D
  Height = 12
  Placement = pos=(0,0,12) rot=(0,0,1;0rad)
  Radius = 2.2
FEATURE [Part::MultiFuse] Fusion103077013  label="M2-screw001"
  Placement = pos=(0,13,30) rot=(0.862856,0.357407,0.357407;1.71777rad)
  Shapes = -> [Cylinder068,Cylinder069]
FEATURE [Part::Feature] Fusion103077013001
  Placement = pos=(-2e-15,-13,30) rot=(-0.281085,0.678598,0.678598;3.68962rad)
  shape: bbox 19.37 x 19.37 x 4.4 mm, 5 faces (baked)
FEATURE [Part::MultiFuse] Fusion103077013002  label="motor-clamp-screws"
  Shapes = -> [Fusion103077013,Fusion103077013001]
FEATURE [Part::Cylinder] Cylinder070
  Angle = 360
  AttacherType = Attacher::AttachEngine3D
  Height = 12
  Placement = pos=(0,0,12) rot=(0,0,1;0rad)
  Radius = 2.2
FEATURE [Part::Cylinder] Cylinder071
  Angle = 360
  AttacherType = Attacher::AttachEngine3D
  Height = 12
  Radius = 1.2
FEATURE [Part::Cylinder] Cylinder072  label="M3-cap-screw-head"
  Angle = 360
  AttacherType = Attacher::AttachEngine3D
  Height = 10
  Placement = pos=(0,15,4) rot=(0,0,1;0rad)
  Radius = 3
FEATURE [Part::FeaturePython] BevelGear002  # WARN: FeaturePython — macro-defined, semantics opaque (R4)
  Placement = pos=(0,0,2.5) rot=(0,0,1;0rad)
  backlash = 0
  beta = 0
  clearance = 0.1
  height = 3
  m = 1
  numpoints = 6
  pitch_angle = 45
  pressure_angle = 20
  reset_origin = true
  teeth = 20
FEATURE [Part::MultiCommon] Common  label="big-gear-a"
  Shapes = -> [BevelGear002,Cylinder054]
FEATURE [Part::MultiCommon] Common005  label="small-gear-1"
  Shapes = -> [Cone,BevelGear001]
FEATURE [Part::MultiFuse] Fusion103077013004005  label="small-gear-2"
  Shapes = -> [Common005,Cylinder057]
FEATURE [Part::MultiFuse] Fusion103077013004006  label="small-gear-cavity"
  Shapes = -> [Cylinder058,Shape001]
FEATURE [Part::Cut] Cut173011005  label="small-gear"
  Base = -> Fusion103077013004005
  Tool = -> Fusion103077013004006
FEATURE [Part::Cylinder] Cylinder073  label="motor-bulge"
  Angle = 360
  AttacherType = Attacher::AttachEngine3D
  Height = 10
  Placement = pos=(0,0,23) rot=(0,0,1;0rad)
  Radius = 9
FEATURE [Part::Cylinder] Cylinder074  label="big-gear-clearance"
  Angle = 360
  AttacherType = Attacher::AttachEngine3D
  Height = 22
  Radius = 12
FEATURE [Part::MultiFuse] Fusion103077013004008  label="motor-clamp-holes-1"
  Shapes = -> [Common004,Fusion103077013002,Box406016]
FEATURE [Part::Cylinder] Cylinder075  label="M3-cap-screw-head001"
  Angle = 360
  AttacherType = Attacher::AttachEngine3D
  Height = 10
  Placement = pos=(0,15,-6) rot=(0,0,1;0rad)
  Radius = 1.7
FEATURE [Part::MultiFuse] Fusion103077013004011  label="M3-cap-screw"
  Placement = pos=(0,0,5) rot=(0,0,1;0rad)
  Shapes = -> [Cylinder075,Cylinder072]
FEATURE [Part::Box] Box406019  label="motor-clamp-print-45"
  AttacherType = Attacher::AttachEngine3D
  Height = 30
  Length = 16.46
  Placement = pos=(-19.23,2.77,20) rot=(0.707107,0.707107,0;1.5708rad)
  Width = 16.46
FEATURE [Part::Feature] Box406008001  label="slot-2"
  Placement = pos=(-10.22,-17.65,0) rot=(0,0,1;2.35619rad)
  shape: bbox 27.22 x 27.22 x 36 mm, 6 faces (baked)
FEATURE [Part::Box] Box406008002  label="Cube339"
  AttacherType = Attacher::AttachEngine3D
  Height = 20
  Length = 23
  Placement = pos=(-1.06066,-15.2028,0) rot=(0,0,1;0.785398rad)
  Width = 20
FEATURE [Part::Fillet] Fillet001
  Base = -> Box406019
  Edges = 1 edges r=3: [Edge3]
FEATURE [Part::MultiFuse] Fusion103077013004012  label="mount-central-hole"
  Shapes = -> [Box406008002,Fillet001]
FEATURE [Part::MultiFuse] Fusion103077013004013  label="finger-slots"
  Shapes = -> [Box406008,Box406008001]
FEATURE [Part::Chamfer] Chamfer024  label="motor-clamp-1"
  Base = -> Box406015
  Edges = 2 edges r=12: [Edge2,Edge6]
FEATURE [Part::MultiFuse] Fusion103077013004014  label="motor-clamp-holes-2"
  Shapes = -> [Fusion103077013004008,Fusion103077013004012]
FEATURE [Part::Chamfer] Chamfer025  label="motor-clamp-2"
  Base = -> Chamfer024
  Edges = 4 edges r=2: [Edge1,Edge4,Edge5,Edge14]
FEATURE [Part::MultiFuse] Fusion103077013004015  label="motor-clamp-holes-3"
  Shapes = -> [Fusion103077013004014,Fusion103077013004013]
FEATURE [Part::MultiFuse] Fusion103077013004016  label="motor-clamp-3"
  Shapes = -> [Chamfer025,Cylinder073]
FEATURE [Part::Cut] Cut173011006  label="motor-clamp-4"
  Base = -> Fusion103077013004016
  Tool = -> Fusion103077013004015
FEATURE [Part::Fillet] Fillet002  label="motor-clamp-5"
  Base = -> Cut173011006
  Edges = 4 edges r=0.7: [Edge102,Edge119,Edge142,Edge146]
FEATURE [Part::Box] Box406008003  label="Cube340"
  AttacherType = Attacher::AttachEngine3D
  Height = 6
  Length = 15
  Placement = pos=(-5,10,2) rot=(0,0,1;0rad)
  Width = 10
FEATURE [Part::Cut] Cut173011007  label="screw-land-1"
  Base = -> Box406008003
  Tool = -> Cylinder074
FEATURE [Part::Cone] Cone001
  Angle = 360
  AttacherType = Attacher::AttachEngine3D
  Height = 9
  Placement = pos=(8.52,8.52,10.5) rot=(0.862856,-0.357407,-0.357407;1.71777rad)
  Radius1 = 9
  Radius2 = 2.5
FEATURE [Part::Cut] Cut173011008  label="Screw-land-2"
  Base = -> Cut173011007
  Tool = -> Cone001
FEATURE [Part::Cut] Cut173011009  label="screw-land-3"
  Base = -> Cut173011008
  Tool = -> Fusion103077013004011
FEATURE [Part::Fillet] Fillet003
  Base = -> Cut173011009
  Edges = 1 edges r=4: [Edge4]
FEATURE [Part::Fillet] Fillet004  label="screw-land-4"
  Base = -> Fillet003
  Edges = 1 edges r=3: [Edge3]
FEATURE [Part::Fillet] Fillet005  label="screw-land-005"
  Base = -> Fillet003
  Edges = 1 edges r=3: [Edge3]
FEATURE [Part::Mirroring] Part__Mirroring002  label="screw-land-005 (Mirror #3)"
  Base = (0,0,0)
  Normal = (1,0,0)
  Placement = pos=(0,0,0) rot=(0,0,1;1.5708rad)
  Source = -> Fillet005
FEATURE [Part::MultiFuse] Fusion103077013004017  label="screw-lands-1"
  Shapes = -> [Fillet004,Part__Mirroring002]
FEATURE [Part::Feature] Fusion103077013004017001  label="screw-lands-2"
  Placement = pos=(0,0,0) rot=(0,0,1;3.14159rad)
  shape: bbox 30 x 30 x 6.628 mm, 26 faces, 2 solids (baked)
FEATURE [Part::MultiFuse] Fusion103077013004017002  label="screw-lands"
  Shapes = -> [Fusion103077013004017001,Fusion103077013004017]
FEATURE [Part::MultiFuse] Fusion103077013004017003  label="motor-clamp-6"
  Shapes = -> [Fillet002,Fusion103077013004017002]
FEATURE [Part::Cut] Cut173011010  label="motor-clamp"
  Base = -> Fusion103077013004017003
  Tool = -> Cylinder059
FEATURE [Part::Box] Box406008004  label="gearbox004"
  AttacherType = Attacher::AttachEngine3D
  Height = 9
  Length = 12
  Placement = pos=(-6,-5,0) rot=(0,0,1;0rad)
  Width = 10
FEATURE [Part::Cylinder] Cylinder076  label="boss002"
  Angle = 360
  AttacherType = Attacher::AttachEngine3D
  Height = 1
  Placement = pos=(0,0,-1) rot=(0,0,1;0rad)
  Radius = 2
FEATURE [Part::Cylinder] Cylinder077
  Angle = 360
  AttacherType = Attacher::AttachEngine3D
  Height = 15
  Placement = pos=(0,0,9) rot=(0,0,1;0rad)
  Radius = 6
FEATURE [Part::Box] Box406008005  label="gearbox005"
  AttacherType = Attacher::AttachEngine3D
  Height = 27
  Length = 16
  Placement = pos=(-8,-5,0) rot=(0,0,1;0rad)
  Width = 10
FEATURE [Part::MultiCommon] Common001  label="motor002"
  Shapes = -> [Cylinder077,Box406008005]
FEATURE [Part::Cylinder] Cylinder078  label="shaft-002"
  Angle = 360
  AttacherType = Attacher::AttachEngine3D
  Height = 10
  Placement = pos=(0,0,-10) rot=(0,0,1;0rad)
  Radius = 1.5
FEATURE [Part::Box] Box406008006  label="Cube341"
  AttacherType = Attacher::AttachEngine3D
  Height = 12
  Length = 10
  Placement = pos=(-5,1,-11) rot=(0,0,1;0rad)
  Width = 10
FEATURE [Part::Cut] Cut001  label="shaft002"
  Base = -> Cylinder078
  Tool = -> Box406008006
FEATURE [Part::MultiFuse] Fusion103077013004017004  label="motor-assembled"
  Placement = pos=(0,0,11) rot=(0,0,-1;0.785398rad)
  Shapes = -> [Box406008004,Cylinder076,Common001,Cut001]
FEATURE [Part::Cylinder] Cylinder079  label="shaft-003"
  Angle = 360
  AttacherType = Attacher::AttachEngine3D
  Height = 10
  Placement = pos=(0,0,-2) rot=(0,0,1;0rad)
  Radius = 1.75
FEATURE [Part::Box] Box406008007  label="Cube342"
  AttacherType = Attacher::AttachEngine3D
  Height = 12
  Length = 10
  Placement = pos=(-5,1.125,-2) rot=(0,0,1;0rad)
  Width = 10
FEATURE [Part::Cut] Cut173011011  label="motor-shaft"
  Base = -> Cylinder079
  Tool = -> Box406008007
FEATURE [Part::Cut] Cut173011012  label="big-gear-2"
  Base = -> Common
  Tool = -> Cut173011011
FEATURE [Part::Box] Box406008008  label="Cube343"
  AttacherType = Attacher::AttachEngine3D
  Height = 2
  Length = 19
  Placement = pos=(-9.5,-9.5,0) rot=(0,0,1;0rad)
  Width = 19
FEATURE [Part::Cylinder] Cylinder080  label="Cylinder078"
  Angle = 360
  AttacherType = Attacher::AttachEngine3D
  Height = 10
  Placement = pos=(0,0,-4) rot=(0,0,1;0rad)
  Radius = 1.8
FEATURE [Part::Cut] Cut173011013  label="filler-plate-1"
  Base = -> Box406008008
  Tool = -> Cylinder080
FEATURE [Part::Chamfer] Chamfer026  label="filler-plate-2"
  Base = -> Cut173011013
  Edges = 1 edges r=0.5: [Edge10]
FEATURE [Part::Chamfer] Chamfer027  label="filler-plate"
  Base = -> Chamfer026
  Edges = 4 edges r=0.5: [Edge10,Edge11,Edge13,Edge15]
FEATURE [Part::Box] Box406008009  label="Cube344"
  AttacherType = Attacher::AttachEngine3D
  Height = 3
  Length = 6
  Placement = pos=(19,19,-7) rot=(0,0,1;0rad)
  Width = 6
FEATURE [Part::Chamfer] Chamfer029  label="grip-1"
  Base = -> Box406008009
  Edges = 2 edges r=1: [Edge2,Edge10]
FEATURE [Part::Chamfer] Chamfer030  label="grip-2"
  Base = -> Chamfer029
  Edges = 1 edges r=1: [Edge1]
FEATURE [Part::Cut] Cut173011016  label="mounting-plate"
  Base = -> Cut139
  Placement = pos=(0,0,0) rot=(1,0,0;3.14159rad)
  Tool = -> Fusion103040
FEATURE [Part::Chamfer] Chamfer032  label="big-gear"
  Base = -> Cut173011012
  Edges = 3 edges r=0.5: [Edge124,Edge125,Edge126]
FEATURE [Part::Feature] Shape002  label="M3-head-cover"
  Placement = pos=(5,5,10.5) rot=(0.862856,-0.357407,-0.357407;1.71777rad)
  shape: bbox 5.347 x 5.347 x 5.25 mm, 8 faces (baked)
FEATURE [Part::Cylinder] Cylinder081  label="M3-screw-drive004"
  Angle = 360
  AttacherType = Attacher::AttachEngine3D
  Height = 20
  Placement = pos=(23.4,23.4,10.5) rot=(0.862856,-0.357407,-0.357407;1.71777rad)
  Radius = 4.5
FEATURE [Part::Feature] Cylinder081001
  Placement = pos=(-23.4,-23.4,10.5) rot=(0.281085,0.678598,0.678598;2.59356rad)
  shape: bbox 20.51 x 20.51 x 9 mm, 3 faces (baked)
FEATURE [Part::MultiFuse] Fusion103077013004017006  label="nut-cavities"
  Shapes = -> [Cylinder081001,Cylinder081]
FEATURE [App::DocumentObjectGroup] Group001  label="Old"
  Group = -> [Cut008,Cut009,Cut015,Cut018,Fusion021,Fusion023,Group,Cut039,Cut028,Cut032,Cut033,Fusion048,Cylinder068,Cylinder069,Cylinder071,Cylinder070,Fusion103077013004017006]
FEATURE [Part::Chamfer] Chamfer  label="finger-1"
  Base = -> Box405
  Edges = 2 edges r=8.5: [Edge3,Edge5]
FEATURE [Part::Cut] Cut173011017  label="finger-2"
  Base = -> Chamfer
  Tool = -> Box406007
FEATURE [Part::Fillet] Fillet  label="finger-3"
  Base = -> Cut173011017
  Edges = 2 edges r=1.5: [Edge8,Edge14]
FEATURE [Part::Chamfer] Chamfer033  label="grip-3"
  Base = -> Chamfer030
  Edges = 3 edges r=1: [Edge4,Edge10,Edge15]
FEATURE [Part::MultiFuse] Fusion103077013004017007  label="finger-4"
  Shapes = -> [Chamfer033,Box404,Fillet]
FEATURE [Part::Fillet] Fillet006  label="finger-5"
  Base = -> Fusion103077013004017007
  Edges = 4 edges r=3: [Edge33,Edge41,Edge51,Edge59]
FEATURE [Part::Cut] Cut173011018  label="finger-6"
  Base = -> Fillet006
  Tool = -> Fusion103077010
FEATURE [Part::Chamfer] Chamfer034  label="finger"
  Base = -> Cut173011018
  Edges = 4 edges r=0.7: [Edge81,Edge82,Edge83,Edge84]
note: 2 file-system paths scrubbed to <path> (originals preserved in the JSON sidecar)
